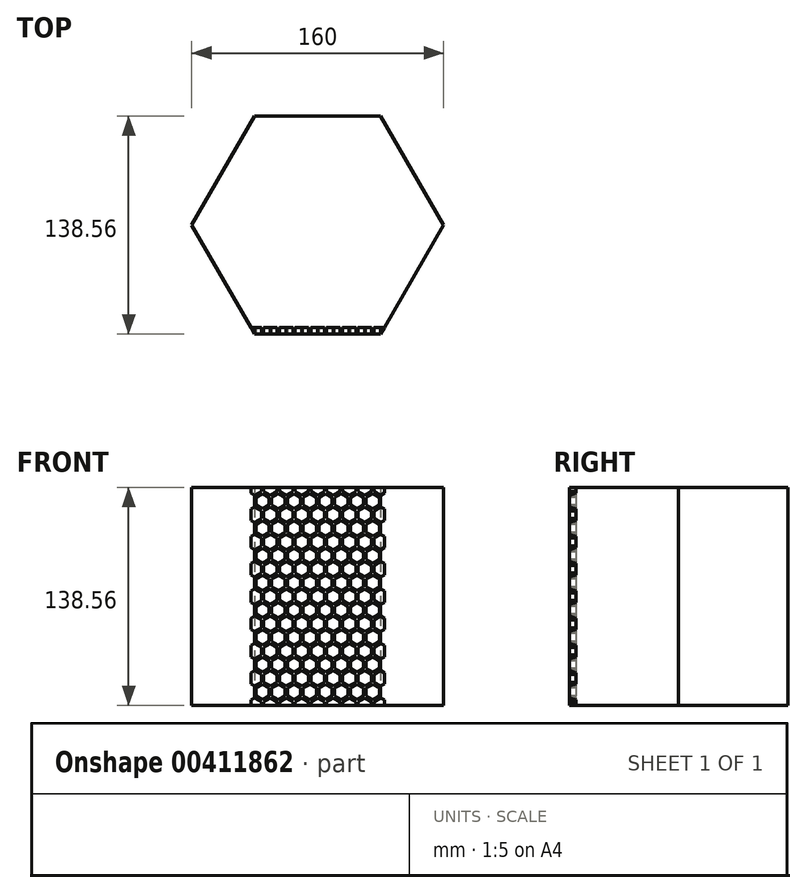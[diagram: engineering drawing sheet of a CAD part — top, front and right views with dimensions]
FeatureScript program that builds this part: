
annotation { "Feature Type Name" : "Feature", "Feature Type Description" : "" }
export const myFeature = defineFeature(function(context is Context, id is Id, definition is map)
    precondition{}
    {
        {
            var Q0;
            Q0=qCreatedBy(makeId("Top.planeOp"),FACE);
            var sketch = newSketch(context, id + "F0", { "sketchPlane" : qUnion([Q0])});
            skCircle(sketch, "E0.cCircle", {"center": v(0, 0) * mm, "radius": 69.28 * mm, "construction": true});
            skLineSegment(sketch, "E0.0", {"start": v(40, -69.28) * mm, "end": v(-40, -69.28) * mm});
            skLineSegment(sketch, "E0.1", {"start": v(-40, -69.28) * mm, "end": v(-80, 0) * mm});
            skLineSegment(sketch, "E0.2", {"start": v(-80, 0) * mm, "end": v(-40, 69.28) * mm});
            skLineSegment(sketch, "E0.3", {"start": v(-40, 69.28) * mm, "end": v(40, 69.28) * mm});
            skLineSegment(sketch, "E0.4", {"start": v(40, 69.28) * mm, "end": v(80, 0) * mm});
            skLineSegment(sketch, "E0.5", {"start": v(80, 0) * mm, "end": v(40, -69.28) * mm});
            skPoint(sketch, "E0.0.midPoint", {"position": v(0, -69.28) * mm});
            skSolve(sketch);
        }
        {
            var Q0;
            Q0=makeQuery(id+"F0.imprint","IMPRINT",FACE,{"disambiguationData":[TD([[makeQuery(id+"F0.imprint","IMPRINT",EDGE,{"derivedFrom":sQuery(id+"F0.wireOp",EDGE,"E0.0")}),-1.0]])]});
            extrude(context, id + "F1", {"entities" : qUnion([Q0]), "depth" : 138.56 * mm});
        }
        {
            var Q0;
            Q0=makeQuery(id+"F1.opExtrude","SWEPT_FACE",FACE,{"disambiguationData":[OSD([sQuery(id+"F0.wireOp",EDGE,"E0.0")])]});
            var sketch = newSketch(context, id + "F2", { "sketchPlane" : qUnion([Q0])});
            skCircle(sketch, "E1.cCircle", {"center": v(-40, 0) * mm, "radius": 4.25 * mm, "construction": true});
            skLineSegment(sketch, "E1.0", {"start": v(-35.75, 2.45) * mm, "end": v(-35.75, -2.45) * mm});
            skLineSegment(sketch, "E1.1", {"start": v(-35.75, -2.45) * mm, "end": v(-40, -4.9) * mm});
            skLineSegment(sketch, "E1.2", {"start": v(-40, -4.9) * mm, "end": v(-44.25, -2.45) * mm});
            skLineSegment(sketch, "E1.3", {"start": v(-44.25, -2.45) * mm, "end": v(-44.25, 2.45) * mm});
            skLineSegment(sketch, "E1.4", {"start": v(-44.25, 2.45) * mm, "end": v(-40, 4.9) * mm});
            skLineSegment(sketch, "E1.5", {"start": v(-40, 4.9) * mm, "end": v(-35.75, 2.45) * mm});
            skPoint(sketch, "E1.0.midPoint", {"position": v(-35.75, 0) * mm});
            skLineSegment(sketch, "E2.1.0.0", {"start": v(-34.25, 2.45) * mm, "end": v(-30, 4.9) * mm});
            skLineSegment(sketch, "E2.1.0.1", {"start": v(-30, 4.9) * mm, "end": v(-25.75, 2.45) * mm});
            skLineSegment(sketch, "E2.1.0.2", {"start": v(-25.75, 2.45) * mm, "end": v(-25.75, -2.45) * mm});
            skLineSegment(sketch, "E2.1.0.3", {"start": v(-25.75, -2.45) * mm, "end": v(-30, -4.9) * mm});
            skLineSegment(sketch, "E2.1.0.4", {"start": v(-30, -4.9) * mm, "end": v(-34.25, -2.45) * mm});
            skLineSegment(sketch, "E2.1.0.5", {"start": v(-34.25, -2.45) * mm, "end": v(-34.25, 2.45) * mm});
            skLineSegment(sketch, "E2.2.0.0", {"start": v(-24.25, 2.45) * mm, "end": v(-20, 4.9) * mm});
            skLineSegment(sketch, "E2.2.0.1", {"start": v(-20, 4.9) * mm, "end": v(-15.75, 2.45) * mm});
            skLineSegment(sketch, "E2.2.0.2", {"start": v(-15.75, 2.45) * mm, "end": v(-15.75, -2.45) * mm});
            skLineSegment(sketch, "E2.2.0.3", {"start": v(-15.75, -2.45) * mm, "end": v(-20, -4.9) * mm});
            skLineSegment(sketch, "E2.2.0.4", {"start": v(-20, -4.9) * mm, "end": v(-24.25, -2.45) * mm});
            skLineSegment(sketch, "E2.2.0.5", {"start": v(-24.25, -2.45) * mm, "end": v(-24.25, 2.45) * mm});
            skLineSegment(sketch, "E2.3.0.0", {"start": v(-14.25, 2.45) * mm, "end": v(-10, 4.9) * mm});
            skLineSegment(sketch, "E2.3.0.1", {"start": v(-10, 4.9) * mm, "end": v(-5.75, 2.45) * mm});
            skLineSegment(sketch, "E2.3.0.2", {"start": v(-5.75, 2.45) * mm, "end": v(-5.75, -2.45) * mm});
            skLineSegment(sketch, "E2.3.0.3", {"start": v(-5.75, -2.45) * mm, "end": v(-10, -4.9) * mm});
            skLineSegment(sketch, "E2.3.0.4", {"start": v(-10, -4.9) * mm, "end": v(-14.25, -2.45) * mm});
            skLineSegment(sketch, "E2.3.0.5", {"start": v(-14.25, -2.45) * mm, "end": v(-14.25, 2.45) * mm});
            skLineSegment(sketch, "E2.4.0.0", {"start": v(-4.25, 2.45) * mm, "end": v(0, 4.9) * mm});
            skLineSegment(sketch, "E2.4.0.1", {"start": v(0, 4.9) * mm, "end": v(4.25, 2.45) * mm});
            skLineSegment(sketch, "E2.4.0.2", {"start": v(4.25, 2.45) * mm, "end": v(4.25, -2.45) * mm});
            skLineSegment(sketch, "E2.4.0.3", {"start": v(4.25, -2.45) * mm, "end": v(0, -4.9) * mm});
            skLineSegment(sketch, "E2.4.0.4", {"start": v(0, -4.9) * mm, "end": v(-4.25, -2.45) * mm});
            skLineSegment(sketch, "E2.4.0.5", {"start": v(-4.25, -2.45) * mm, "end": v(-4.25, 2.45) * mm});
            skLineSegment(sketch, "E2.direction1", {"start": v(-44.25, -2.45) * mm, "end": v(-34.25, -2.45) * mm, "construction": true});
            skLineSegment(sketch, "E2.direction2", {"start": v(-44.25, -2.45) * mm, "end": v(-44.25, 14.87) * mm, "construction": true});
            skLineSegment(sketch, "E3.0.5.0", {"start": v(5.75, 2.45) * mm, "end": v(10, 4.9) * mm});
            skLineSegment(sketch, "E3.3.5.0", {"start": v(10, 4.9) * mm, "end": v(14.25, 2.45) * mm});
            skLineSegment(sketch, "E3.6.5.0", {"start": v(14.25, 2.45) * mm, "end": v(14.25, -2.45) * mm});
            skLineSegment(sketch, "E3.9.5.0", {"start": v(14.25, -2.45) * mm, "end": v(10, -4.9) * mm});
            skLineSegment(sketch, "E3.12.5.0", {"start": v(10, -4.9) * mm, "end": v(5.75, -2.45) * mm});
            skLineSegment(sketch, "E3.15.5.0", {"start": v(5.75, -2.45) * mm, "end": v(5.75, 2.45) * mm});
            skLineSegment(sketch, "E3.0.6.0", {"start": v(15.75, 2.45) * mm, "end": v(20, 4.9) * mm});
            skLineSegment(sketch, "E3.3.6.0", {"start": v(20, 4.9) * mm, "end": v(24.25, 2.45) * mm});
            skLineSegment(sketch, "E3.6.6.0", {"start": v(24.25, 2.45) * mm, "end": v(24.25, -2.45) * mm});
            skLineSegment(sketch, "E3.9.6.0", {"start": v(24.25, -2.45) * mm, "end": v(20, -4.9) * mm});
            skLineSegment(sketch, "E3.12.6.0", {"start": v(20, -4.9) * mm, "end": v(15.75, -2.45) * mm});
            skLineSegment(sketch, "E3.15.6.0", {"start": v(15.75, -2.45) * mm, "end": v(15.75, 2.45) * mm});
            skLineSegment(sketch, "E3.0.7.0", {"start": v(25.75, 2.45) * mm, "end": v(30, 4.9) * mm});
            skLineSegment(sketch, "E3.3.7.0", {"start": v(30, 4.9) * mm, "end": v(34.25, 2.45) * mm});
            skLineSegment(sketch, "E3.6.7.0", {"start": v(34.25, 2.45) * mm, "end": v(34.25, -2.45) * mm});
            skLineSegment(sketch, "E3.9.7.0", {"start": v(34.25, -2.45) * mm, "end": v(30, -4.9) * mm});
            skLineSegment(sketch, "E3.12.7.0", {"start": v(30, -4.9) * mm, "end": v(25.75, -2.45) * mm});
            skLineSegment(sketch, "E3.15.7.0", {"start": v(25.75, -2.45) * mm, "end": v(25.75, 2.45) * mm});
            skLineSegment(sketch, "E4.0.8.0", {"start": v(35.75, 2.45) * mm, "end": v(40, 4.9) * mm});
            skLineSegment(sketch, "E4.3.8.0", {"start": v(40, 4.9) * mm, "end": v(44.25, 2.45) * mm});
            skLineSegment(sketch, "E4.6.8.0", {"start": v(44.25, 2.45) * mm, "end": v(44.25, -2.45) * mm});
            skLineSegment(sketch, "E4.9.8.0", {"start": v(44.25, -2.45) * mm, "end": v(40, -4.9) * mm});
            skLineSegment(sketch, "E4.12.8.0", {"start": v(40, -4.9) * mm, "end": v(35.75, -2.45) * mm});
            skLineSegment(sketch, "E4.15.8.0", {"start": v(35.75, -2.45) * mm, "end": v(35.75, 2.45) * mm});
            skCircle(sketch, "E5.cCircle", {"center": v(-35, 8.66) * mm, "radius": 4.25 * mm, "construction": true});
            skLineSegment(sketch, "E5.0", {"start": v(-30.75, 11.11) * mm, "end": v(-30.75, 6.2) * mm});
            skLineSegment(sketch, "E5.1", {"start": v(-30.75, 6.2) * mm, "end": v(-35, 3.75) * mm});
            skLineSegment(sketch, "E5.2", {"start": v(-35, 3.75) * mm, "end": v(-39.25, 6.2) * mm});
            skLineSegment(sketch, "E5.3", {"start": v(-39.25, 6.2) * mm, "end": v(-39.25, 11.11) * mm});
            skLineSegment(sketch, "E5.4", {"start": v(-39.25, 11.11) * mm, "end": v(-35, 13.57) * mm});
            skLineSegment(sketch, "E5.5", {"start": v(-35, 13.57) * mm, "end": v(-30.75, 11.11) * mm});
            skPoint(sketch, "E5.0.midPoint", {"position": v(-30.75, 8.66) * mm});
            skLineSegment(sketch, "E6.0.0.1", {"start": v(-44.25, 19.77) * mm, "end": v(-40, 22.23) * mm});
            skLineSegment(sketch, "E6.3.0.1", {"start": v(-40, 22.23) * mm, "end": v(-35.75, 19.77) * mm});
            skLineSegment(sketch, "E6.6.0.1", {"start": v(-35.75, 19.77) * mm, "end": v(-35.75, 14.87) * mm});
            skLineSegment(sketch, "E6.9.0.1", {"start": v(-35.75, 14.87) * mm, "end": v(-40, 12.41) * mm});
            skLineSegment(sketch, "E6.12.0.1", {"start": v(-40, 12.41) * mm, "end": v(-44.25, 14.87) * mm});
            skLineSegment(sketch, "E6.15.0.1", {"start": v(-44.25, 14.87) * mm, "end": v(-44.25, 19.77) * mm});
            skLineSegment(sketch, "E6.0.0.2", {"start": v(-44.25, 37.1) * mm, "end": v(-40, 39.55) * mm});
            skLineSegment(sketch, "E6.3.0.2", {"start": v(-40, 39.55) * mm, "end": v(-35.75, 37.1) * mm});
            skLineSegment(sketch, "E6.6.0.2", {"start": v(-35.75, 37.1) * mm, "end": v(-35.75, 32.19) * mm});
            skLineSegment(sketch, "E6.9.0.2", {"start": v(-35.75, 32.19) * mm, "end": v(-40, 29.73) * mm});
            skLineSegment(sketch, "E6.12.0.2", {"start": v(-40, 29.73) * mm, "end": v(-44.25, 32.19) * mm});
            skLineSegment(sketch, "E6.15.0.2", {"start": v(-44.25, 32.19) * mm, "end": v(-44.25, 37.1) * mm});
            skLineSegment(sketch, "E6.0.0.3", {"start": v(-44.25, 54.42) * mm, "end": v(-40, 56.87) * mm});
            skLineSegment(sketch, "E6.3.0.3", {"start": v(-40, 56.87) * mm, "end": v(-35.75, 54.42) * mm});
            skLineSegment(sketch, "E6.6.0.3", {"start": v(-35.75, 54.42) * mm, "end": v(-35.75, 49.5) * mm});
            skLineSegment(sketch, "E6.9.0.3", {"start": v(-35.75, 49.5) * mm, "end": v(-40, 47.05) * mm});
            skLineSegment(sketch, "E6.12.0.3", {"start": v(-40, 47.05) * mm, "end": v(-44.25, 49.5) * mm});
            skLineSegment(sketch, "E6.15.0.3", {"start": v(-44.25, 49.5) * mm, "end": v(-44.25, 54.42) * mm});
            skLineSegment(sketch, "E6.0.0.4", {"start": v(-44.25, 71.74) * mm, "end": v(-40, 74.19) * mm});
            skLineSegment(sketch, "E6.3.0.4", {"start": v(-40, 74.19) * mm, "end": v(-35.75, 71.74) * mm});
            skLineSegment(sketch, "E6.6.0.4", {"start": v(-35.75, 71.74) * mm, "end": v(-35.75, 66.83) * mm});
            skLineSegment(sketch, "E6.9.0.4", {"start": v(-35.75, 66.83) * mm, "end": v(-40, 64.37) * mm});
            skLineSegment(sketch, "E6.12.0.4", {"start": v(-40, 64.37) * mm, "end": v(-44.25, 66.83) * mm});
            skLineSegment(sketch, "E6.15.0.4", {"start": v(-44.25, 66.83) * mm, "end": v(-44.25, 71.74) * mm});
            skLineSegment(sketch, "E6.0.0.5", {"start": v(-44.25, 89.06) * mm, "end": v(-40, 91.51) * mm});
            skLineSegment(sketch, "E6.3.0.5", {"start": v(-40, 91.51) * mm, "end": v(-35.75, 89.06) * mm});
            skLineSegment(sketch, "E6.6.0.5", {"start": v(-35.75, 89.06) * mm, "end": v(-35.75, 84.15) * mm});
            skLineSegment(sketch, "E6.9.0.5", {"start": v(-35.75, 84.15) * mm, "end": v(-40, 81.7) * mm});
            skLineSegment(sketch, "E6.12.0.5", {"start": v(-40, 81.7) * mm, "end": v(-44.25, 84.15) * mm});
            skLineSegment(sketch, "E6.15.0.5", {"start": v(-44.25, 84.15) * mm, "end": v(-44.25, 89.06) * mm});
            skLineSegment(sketch, "E6.0.0.6", {"start": v(-44.25, 106.38) * mm, "end": v(-40, 108.83) * mm});
            skLineSegment(sketch, "E6.3.0.6", {"start": v(-40, 108.83) * mm, "end": v(-35.75, 106.38) * mm});
            skLineSegment(sketch, "E6.6.0.6", {"start": v(-35.75, 106.38) * mm, "end": v(-35.75, 101.47) * mm});
            skLineSegment(sketch, "E6.9.0.6", {"start": v(-35.75, 101.47) * mm, "end": v(-40, 99.02) * mm});
            skLineSegment(sketch, "E6.12.0.6", {"start": v(-40, 99.02) * mm, "end": v(-44.25, 101.47) * mm});
            skLineSegment(sketch, "E6.15.0.6", {"start": v(-44.25, 101.47) * mm, "end": v(-44.25, 106.38) * mm});
            skLineSegment(sketch, "E6.0.0.7", {"start": v(-44.25, 123.7) * mm, "end": v(-40, 126.15) * mm});
            skLineSegment(sketch, "E6.3.0.7", {"start": v(-40, 126.15) * mm, "end": v(-35.75, 123.7) * mm});
            skLineSegment(sketch, "E6.6.0.7", {"start": v(-35.75, 123.7) * mm, "end": v(-35.75, 118.79) * mm});
            skLineSegment(sketch, "E6.9.0.7", {"start": v(-35.75, 118.79) * mm, "end": v(-40, 116.34) * mm});
            skLineSegment(sketch, "E6.12.0.7", {"start": v(-40, 116.34) * mm, "end": v(-44.25, 118.79) * mm});
            skLineSegment(sketch, "E6.15.0.7", {"start": v(-44.25, 118.79) * mm, "end": v(-44.25, 123.7) * mm});
            skLineSegment(sketch, "E6.0.0.8", {"start": v(-44.25, 141.02) * mm, "end": v(-40, 143.47) * mm});
            skLineSegment(sketch, "E6.3.0.8", {"start": v(-40, 143.47) * mm, "end": v(-35.75, 141.02) * mm});
            skLineSegment(sketch, "E6.6.0.8", {"start": v(-35.75, 141.02) * mm, "end": v(-35.75, 136.11) * mm});
            skLineSegment(sketch, "E6.9.0.8", {"start": v(-35.75, 136.11) * mm, "end": v(-40, 133.66) * mm});
            skLineSegment(sketch, "E6.12.0.8", {"start": v(-40, 133.66) * mm, "end": v(-44.25, 136.11) * mm});
            skLineSegment(sketch, "E6.15.0.8", {"start": v(-44.25, 136.11) * mm, "end": v(-44.25, 141.02) * mm});
            skLineSegment(sketch, "E6.0.1.1", {"start": v(-34.25, 19.77) * mm, "end": v(-30, 22.23) * mm});
            skLineSegment(sketch, "E6.3.1.1", {"start": v(-30, 22.23) * mm, "end": v(-25.75, 19.77) * mm});
            skLineSegment(sketch, "E6.6.1.1", {"start": v(-25.75, 19.77) * mm, "end": v(-25.75, 14.87) * mm});
            skLineSegment(sketch, "E6.9.1.1", {"start": v(-25.75, 14.87) * mm, "end": v(-30, 12.41) * mm});
            skLineSegment(sketch, "E6.12.1.1", {"start": v(-30, 12.41) * mm, "end": v(-34.25, 14.87) * mm});
            skLineSegment(sketch, "E6.15.1.1", {"start": v(-34.25, 14.87) * mm, "end": v(-34.25, 19.77) * mm});
            skLineSegment(sketch, "E6.0.1.2", {"start": v(-34.25, 37.1) * mm, "end": v(-30, 39.55) * mm});
            skLineSegment(sketch, "E6.3.1.2", {"start": v(-30, 39.55) * mm, "end": v(-25.75, 37.1) * mm});
            skLineSegment(sketch, "E6.6.1.2", {"start": v(-25.75, 37.1) * mm, "end": v(-25.75, 32.19) * mm});
            skLineSegment(sketch, "E6.9.1.2", {"start": v(-25.75, 32.19) * mm, "end": v(-30, 29.73) * mm});
            skLineSegment(sketch, "E6.12.1.2", {"start": v(-30, 29.73) * mm, "end": v(-34.25, 32.19) * mm});
            skLineSegment(sketch, "E6.15.1.2", {"start": v(-34.25, 32.19) * mm, "end": v(-34.25, 37.1) * mm});
            skLineSegment(sketch, "E6.0.1.3", {"start": v(-34.25, 54.42) * mm, "end": v(-30, 56.87) * mm});
            skLineSegment(sketch, "E6.3.1.3", {"start": v(-30, 56.87) * mm, "end": v(-25.75, 54.42) * mm});
            skLineSegment(sketch, "E6.6.1.3", {"start": v(-25.75, 54.42) * mm, "end": v(-25.75, 49.5) * mm});
            skLineSegment(sketch, "E6.9.1.3", {"start": v(-25.75, 49.5) * mm, "end": v(-30, 47.05) * mm});
            skLineSegment(sketch, "E6.12.1.3", {"start": v(-30, 47.05) * mm, "end": v(-34.25, 49.5) * mm});
            skLineSegment(sketch, "E6.15.1.3", {"start": v(-34.25, 49.5) * mm, "end": v(-34.25, 54.42) * mm});
            skLineSegment(sketch, "E6.0.1.4", {"start": v(-34.25, 71.74) * mm, "end": v(-30, 74.19) * mm});
            skLineSegment(sketch, "E6.3.1.4", {"start": v(-30, 74.19) * mm, "end": v(-25.75, 71.74) * mm});
            skLineSegment(sketch, "E6.6.1.4", {"start": v(-25.75, 71.74) * mm, "end": v(-25.75, 66.83) * mm});
            skLineSegment(sketch, "E6.9.1.4", {"start": v(-25.75, 66.83) * mm, "end": v(-30, 64.37) * mm});
            skLineSegment(sketch, "E6.12.1.4", {"start": v(-30, 64.37) * mm, "end": v(-34.25, 66.83) * mm});
            skLineSegment(sketch, "E6.15.1.4", {"start": v(-34.25, 66.83) * mm, "end": v(-34.25, 71.74) * mm});
            skLineSegment(sketch, "E6.0.1.5", {"start": v(-34.25, 89.06) * mm, "end": v(-30, 91.51) * mm});
            skLineSegment(sketch, "E6.3.1.5", {"start": v(-30, 91.51) * mm, "end": v(-25.75, 89.06) * mm});
            skLineSegment(sketch, "E6.6.1.5", {"start": v(-25.75, 89.06) * mm, "end": v(-25.75, 84.15) * mm});
            skLineSegment(sketch, "E6.9.1.5", {"start": v(-25.75, 84.15) * mm, "end": v(-30, 81.7) * mm});
            skLineSegment(sketch, "E6.12.1.5", {"start": v(-30, 81.7) * mm, "end": v(-34.25, 84.15) * mm});
            skLineSegment(sketch, "E6.15.1.5", {"start": v(-34.25, 84.15) * mm, "end": v(-34.25, 89.06) * mm});
            skLineSegment(sketch, "E6.0.1.6", {"start": v(-34.25, 106.38) * mm, "end": v(-30, 108.83) * mm});
            skLineSegment(sketch, "E6.3.1.6", {"start": v(-30, 108.83) * mm, "end": v(-25.75, 106.38) * mm});
            skLineSegment(sketch, "E6.6.1.6", {"start": v(-25.75, 106.38) * mm, "end": v(-25.75, 101.47) * mm});
            skLineSegment(sketch, "E6.9.1.6", {"start": v(-25.75, 101.47) * mm, "end": v(-30, 99.02) * mm});
            skLineSegment(sketch, "E6.12.1.6", {"start": v(-30, 99.02) * mm, "end": v(-34.25, 101.47) * mm});
            skLineSegment(sketch, "E6.15.1.6", {"start": v(-34.25, 101.47) * mm, "end": v(-34.25, 106.38) * mm});
            skLineSegment(sketch, "E6.0.1.7", {"start": v(-34.25, 123.7) * mm, "end": v(-30, 126.15) * mm});
            skLineSegment(sketch, "E6.3.1.7", {"start": v(-30, 126.15) * mm, "end": v(-25.75, 123.7) * mm});
            skLineSegment(sketch, "E6.6.1.7", {"start": v(-25.75, 123.7) * mm, "end": v(-25.75, 118.79) * mm});
            skLineSegment(sketch, "E6.9.1.7", {"start": v(-25.75, 118.79) * mm, "end": v(-30, 116.34) * mm});
            skLineSegment(sketch, "E6.12.1.7", {"start": v(-30, 116.34) * mm, "end": v(-34.25, 118.79) * mm});
            skLineSegment(sketch, "E6.15.1.7", {"start": v(-34.25, 118.79) * mm, "end": v(-34.25, 123.7) * mm});
            skLineSegment(sketch, "E6.0.1.8", {"start": v(-34.25, 141.02) * mm, "end": v(-30, 143.47) * mm});
            skLineSegment(sketch, "E6.3.1.8", {"start": v(-30, 143.47) * mm, "end": v(-25.75, 141.02) * mm});
            skLineSegment(sketch, "E6.6.1.8", {"start": v(-25.75, 141.02) * mm, "end": v(-25.75, 136.11) * mm});
            skLineSegment(sketch, "E6.9.1.8", {"start": v(-25.75, 136.11) * mm, "end": v(-30, 133.66) * mm});
            skLineSegment(sketch, "E6.12.1.8", {"start": v(-30, 133.66) * mm, "end": v(-34.25, 136.11) * mm});
            skLineSegment(sketch, "E6.15.1.8", {"start": v(-34.25, 136.11) * mm, "end": v(-34.25, 141.02) * mm});
            skLineSegment(sketch, "E6.0.2.1", {"start": v(-24.25, 19.77) * mm, "end": v(-20, 22.23) * mm});
            skLineSegment(sketch, "E6.3.2.1", {"start": v(-20, 22.23) * mm, "end": v(-15.75, 19.77) * mm});
            skLineSegment(sketch, "E6.6.2.1", {"start": v(-15.75, 19.77) * mm, "end": v(-15.75, 14.87) * mm});
            skLineSegment(sketch, "E6.9.2.1", {"start": v(-15.75, 14.87) * mm, "end": v(-20, 12.41) * mm});
            skLineSegment(sketch, "E6.12.2.1", {"start": v(-20, 12.41) * mm, "end": v(-24.25, 14.87) * mm});
            skLineSegment(sketch, "E6.15.2.1", {"start": v(-24.25, 14.87) * mm, "end": v(-24.25, 19.77) * mm});
            skLineSegment(sketch, "E6.0.2.2", {"start": v(-24.25, 37.1) * mm, "end": v(-20, 39.55) * mm});
            skLineSegment(sketch, "E6.3.2.2", {"start": v(-20, 39.55) * mm, "end": v(-15.75, 37.1) * mm});
            skLineSegment(sketch, "E6.6.2.2", {"start": v(-15.75, 37.1) * mm, "end": v(-15.75, 32.19) * mm});
            skLineSegment(sketch, "E6.9.2.2", {"start": v(-15.75, 32.19) * mm, "end": v(-20, 29.73) * mm});
            skLineSegment(sketch, "E6.12.2.2", {"start": v(-20, 29.73) * mm, "end": v(-24.25, 32.19) * mm});
            skLineSegment(sketch, "E6.15.2.2", {"start": v(-24.25, 32.19) * mm, "end": v(-24.25, 37.1) * mm});
            skLineSegment(sketch, "E6.0.2.3", {"start": v(-24.25, 54.42) * mm, "end": v(-20, 56.87) * mm});
            skLineSegment(sketch, "E6.3.2.3", {"start": v(-20, 56.87) * mm, "end": v(-15.75, 54.42) * mm});
            skLineSegment(sketch, "E6.6.2.3", {"start": v(-15.75, 54.42) * mm, "end": v(-15.75, 49.5) * mm});
            skLineSegment(sketch, "E6.9.2.3", {"start": v(-15.75, 49.5) * mm, "end": v(-20, 47.05) * mm});
            skLineSegment(sketch, "E6.12.2.3", {"start": v(-20, 47.05) * mm, "end": v(-24.25, 49.5) * mm});
            skLineSegment(sketch, "E6.15.2.3", {"start": v(-24.25, 49.5) * mm, "end": v(-24.25, 54.42) * mm});
            skLineSegment(sketch, "E6.0.2.4", {"start": v(-24.25, 71.74) * mm, "end": v(-20, 74.19) * mm});
            skLineSegment(sketch, "E6.3.2.4", {"start": v(-20, 74.19) * mm, "end": v(-15.75, 71.74) * mm});
            skLineSegment(sketch, "E6.6.2.4", {"start": v(-15.75, 71.74) * mm, "end": v(-15.75, 66.83) * mm});
            skLineSegment(sketch, "E6.9.2.4", {"start": v(-15.75, 66.83) * mm, "end": v(-20, 64.37) * mm});
            skLineSegment(sketch, "E6.12.2.4", {"start": v(-20, 64.37) * mm, "end": v(-24.25, 66.83) * mm});
            skLineSegment(sketch, "E6.15.2.4", {"start": v(-24.25, 66.83) * mm, "end": v(-24.25, 71.74) * mm});
            skLineSegment(sketch, "E6.0.2.5", {"start": v(-24.25, 89.06) * mm, "end": v(-20, 91.51) * mm});
            skLineSegment(sketch, "E6.3.2.5", {"start": v(-20, 91.51) * mm, "end": v(-15.75, 89.06) * mm});
            skLineSegment(sketch, "E6.6.2.5", {"start": v(-15.75, 89.06) * mm, "end": v(-15.75, 84.15) * mm});
            skLineSegment(sketch, "E6.9.2.5", {"start": v(-15.75, 84.15) * mm, "end": v(-20, 81.7) * mm});
            skLineSegment(sketch, "E6.12.2.5", {"start": v(-20, 81.7) * mm, "end": v(-24.25, 84.15) * mm});
            skLineSegment(sketch, "E6.15.2.5", {"start": v(-24.25, 84.15) * mm, "end": v(-24.25, 89.06) * mm});
            skLineSegment(sketch, "E6.0.2.6", {"start": v(-24.25, 106.38) * mm, "end": v(-20, 108.83) * mm});
            skLineSegment(sketch, "E6.3.2.6", {"start": v(-20, 108.83) * mm, "end": v(-15.75, 106.38) * mm});
            skLineSegment(sketch, "E6.6.2.6", {"start": v(-15.75, 106.38) * mm, "end": v(-15.75, 101.47) * mm});
            skLineSegment(sketch, "E6.9.2.6", {"start": v(-15.75, 101.47) * mm, "end": v(-20, 99.02) * mm});
            skLineSegment(sketch, "E6.12.2.6", {"start": v(-20, 99.02) * mm, "end": v(-24.25, 101.47) * mm});
            skLineSegment(sketch, "E6.15.2.6", {"start": v(-24.25, 101.47) * mm, "end": v(-24.25, 106.38) * mm});
            skLineSegment(sketch, "E6.0.2.7", {"start": v(-24.25, 123.7) * mm, "end": v(-20, 126.15) * mm});
            skLineSegment(sketch, "E6.3.2.7", {"start": v(-20, 126.15) * mm, "end": v(-15.75, 123.7) * mm});
            skLineSegment(sketch, "E6.6.2.7", {"start": v(-15.75, 123.7) * mm, "end": v(-15.75, 118.79) * mm});
            skLineSegment(sketch, "E6.9.2.7", {"start": v(-15.75, 118.79) * mm, "end": v(-20, 116.34) * mm});
            skLineSegment(sketch, "E6.12.2.7", {"start": v(-20, 116.34) * mm, "end": v(-24.25, 118.79) * mm});
            skLineSegment(sketch, "E6.15.2.7", {"start": v(-24.25, 118.79) * mm, "end": v(-24.25, 123.7) * mm});
            skLineSegment(sketch, "E6.0.2.8", {"start": v(-24.25, 141.02) * mm, "end": v(-20, 143.47) * mm});
            skLineSegment(sketch, "E6.3.2.8", {"start": v(-20, 143.47) * mm, "end": v(-15.75, 141.02) * mm});
            skLineSegment(sketch, "E6.6.2.8", {"start": v(-15.75, 141.02) * mm, "end": v(-15.75, 136.11) * mm});
            skLineSegment(sketch, "E6.9.2.8", {"start": v(-15.75, 136.11) * mm, "end": v(-20, 133.66) * mm});
            skLineSegment(sketch, "E6.12.2.8", {"start": v(-20, 133.66) * mm, "end": v(-24.25, 136.11) * mm});
            skLineSegment(sketch, "E6.15.2.8", {"start": v(-24.25, 136.11) * mm, "end": v(-24.25, 141.02) * mm});
            skLineSegment(sketch, "E6.0.3.1", {"start": v(-14.25, 19.77) * mm, "end": v(-10, 22.23) * mm});
            skLineSegment(sketch, "E6.3.3.1", {"start": v(-10, 22.23) * mm, "end": v(-5.75, 19.77) * mm});
            skLineSegment(sketch, "E6.6.3.1", {"start": v(-5.75, 19.77) * mm, "end": v(-5.75, 14.87) * mm});
            skLineSegment(sketch, "E6.9.3.1", {"start": v(-5.75, 14.87) * mm, "end": v(-10, 12.41) * mm});
            skLineSegment(sketch, "E6.12.3.1", {"start": v(-10, 12.41) * mm, "end": v(-14.25, 14.87) * mm});
            skLineSegment(sketch, "E6.15.3.1", {"start": v(-14.25, 14.87) * mm, "end": v(-14.25, 19.77) * mm});
            skLineSegment(sketch, "E6.0.3.2", {"start": v(-14.25, 37.1) * mm, "end": v(-10, 39.55) * mm});
            skLineSegment(sketch, "E6.3.3.2", {"start": v(-10, 39.55) * mm, "end": v(-5.75, 37.1) * mm});
            skLineSegment(sketch, "E6.6.3.2", {"start": v(-5.75, 37.1) * mm, "end": v(-5.75, 32.19) * mm});
            skLineSegment(sketch, "E6.9.3.2", {"start": v(-5.75, 32.19) * mm, "end": v(-10, 29.73) * mm});
            skLineSegment(sketch, "E6.12.3.2", {"start": v(-10, 29.73) * mm, "end": v(-14.25, 32.19) * mm});
            skLineSegment(sketch, "E6.15.3.2", {"start": v(-14.25, 32.19) * mm, "end": v(-14.25, 37.1) * mm});
            skLineSegment(sketch, "E6.0.3.3", {"start": v(-14.25, 54.42) * mm, "end": v(-10, 56.87) * mm});
            skLineSegment(sketch, "E6.3.3.3", {"start": v(-10, 56.87) * mm, "end": v(-5.75, 54.42) * mm});
            skLineSegment(sketch, "E6.6.3.3", {"start": v(-5.75, 54.42) * mm, "end": v(-5.75, 49.5) * mm});
            skLineSegment(sketch, "E6.9.3.3", {"start": v(-5.75, 49.5) * mm, "end": v(-10, 47.05) * mm});
            skLineSegment(sketch, "E6.12.3.3", {"start": v(-10, 47.05) * mm, "end": v(-14.25, 49.5) * mm});
            skLineSegment(sketch, "E6.15.3.3", {"start": v(-14.25, 49.5) * mm, "end": v(-14.25, 54.42) * mm});
            skLineSegment(sketch, "E6.0.3.4", {"start": v(-14.25, 71.74) * mm, "end": v(-10, 74.19) * mm});
            skLineSegment(sketch, "E6.3.3.4", {"start": v(-10, 74.19) * mm, "end": v(-5.75, 71.74) * mm});
            skLineSegment(sketch, "E6.6.3.4", {"start": v(-5.75, 71.74) * mm, "end": v(-5.75, 66.83) * mm});
            skLineSegment(sketch, "E6.9.3.4", {"start": v(-5.75, 66.83) * mm, "end": v(-10, 64.37) * mm});
            skLineSegment(sketch, "E6.12.3.4", {"start": v(-10, 64.37) * mm, "end": v(-14.25, 66.83) * mm});
            skLineSegment(sketch, "E6.15.3.4", {"start": v(-14.25, 66.83) * mm, "end": v(-14.25, 71.74) * mm});
            skLineSegment(sketch, "E6.0.3.5", {"start": v(-14.25, 89.06) * mm, "end": v(-10, 91.51) * mm});
            skLineSegment(sketch, "E6.3.3.5", {"start": v(-10, 91.51) * mm, "end": v(-5.75, 89.06) * mm});
            skLineSegment(sketch, "E6.6.3.5", {"start": v(-5.75, 89.06) * mm, "end": v(-5.75, 84.15) * mm});
            skLineSegment(sketch, "E6.9.3.5", {"start": v(-5.75, 84.15) * mm, "end": v(-10, 81.7) * mm});
            skLineSegment(sketch, "E6.12.3.5", {"start": v(-10, 81.7) * mm, "end": v(-14.25, 84.15) * mm});
            skLineSegment(sketch, "E6.15.3.5", {"start": v(-14.25, 84.15) * mm, "end": v(-14.25, 89.06) * mm});
            skLineSegment(sketch, "E6.0.3.6", {"start": v(-14.25, 106.38) * mm, "end": v(-10, 108.83) * mm});
            skLineSegment(sketch, "E6.3.3.6", {"start": v(-10, 108.83) * mm, "end": v(-5.75, 106.38) * mm});
            skLineSegment(sketch, "E6.6.3.6", {"start": v(-5.75, 106.38) * mm, "end": v(-5.75, 101.47) * mm});
            skLineSegment(sketch, "E6.9.3.6", {"start": v(-5.75, 101.47) * mm, "end": v(-10, 99.02) * mm});
            skLineSegment(sketch, "E6.12.3.6", {"start": v(-10, 99.02) * mm, "end": v(-14.25, 101.47) * mm});
            skLineSegment(sketch, "E6.15.3.6", {"start": v(-14.25, 101.47) * mm, "end": v(-14.25, 106.38) * mm});
            skLineSegment(sketch, "E6.0.3.7", {"start": v(-14.25, 123.7) * mm, "end": v(-10, 126.15) * mm});
            skLineSegment(sketch, "E6.3.3.7", {"start": v(-10, 126.15) * mm, "end": v(-5.75, 123.7) * mm});
            skLineSegment(sketch, "E6.6.3.7", {"start": v(-5.75, 123.7) * mm, "end": v(-5.75, 118.79) * mm});
            skLineSegment(sketch, "E6.9.3.7", {"start": v(-5.75, 118.79) * mm, "end": v(-10, 116.34) * mm});
            skLineSegment(sketch, "E6.12.3.7", {"start": v(-10, 116.34) * mm, "end": v(-14.25, 118.79) * mm});
            skLineSegment(sketch, "E6.15.3.7", {"start": v(-14.25, 118.79) * mm, "end": v(-14.25, 123.7) * mm});
            skLineSegment(sketch, "E6.0.3.8", {"start": v(-14.25, 141.02) * mm, "end": v(-10, 143.47) * mm});
            skLineSegment(sketch, "E6.3.3.8", {"start": v(-10, 143.47) * mm, "end": v(-5.75, 141.02) * mm});
            skLineSegment(sketch, "E6.6.3.8", {"start": v(-5.75, 141.02) * mm, "end": v(-5.75, 136.11) * mm});
            skLineSegment(sketch, "E6.9.3.8", {"start": v(-5.75, 136.11) * mm, "end": v(-10, 133.66) * mm});
            skLineSegment(sketch, "E6.12.3.8", {"start": v(-10, 133.66) * mm, "end": v(-14.25, 136.11) * mm});
            skLineSegment(sketch, "E6.15.3.8", {"start": v(-14.25, 136.11) * mm, "end": v(-14.25, 141.02) * mm});
            skLineSegment(sketch, "E6.0.4.1", {"start": v(-4.25, 19.77) * mm, "end": v(0, 22.23) * mm});
            skLineSegment(sketch, "E6.3.4.1", {"start": v(0, 22.23) * mm, "end": v(4.25, 19.77) * mm});
            skLineSegment(sketch, "E6.6.4.1", {"start": v(4.25, 19.77) * mm, "end": v(4.25, 14.87) * mm});
            skLineSegment(sketch, "E6.9.4.1", {"start": v(4.25, 14.87) * mm, "end": v(0, 12.41) * mm});
            skLineSegment(sketch, "E6.12.4.1", {"start": v(0, 12.41) * mm, "end": v(-4.25, 14.87) * mm});
            skLineSegment(sketch, "E6.15.4.1", {"start": v(-4.25, 14.87) * mm, "end": v(-4.25, 19.77) * mm});
            skLineSegment(sketch, "E6.0.4.2", {"start": v(-4.25, 37.1) * mm, "end": v(0, 39.55) * mm});
            skLineSegment(sketch, "E6.3.4.2", {"start": v(0, 39.55) * mm, "end": v(4.25, 37.1) * mm});
            skLineSegment(sketch, "E6.6.4.2", {"start": v(4.25, 37.1) * mm, "end": v(4.25, 32.19) * mm});
            skLineSegment(sketch, "E6.9.4.2", {"start": v(4.25, 32.19) * mm, "end": v(0, 29.73) * mm});
            skLineSegment(sketch, "E6.12.4.2", {"start": v(0, 29.73) * mm, "end": v(-4.25, 32.19) * mm});
            skLineSegment(sketch, "E6.15.4.2", {"start": v(-4.25, 32.19) * mm, "end": v(-4.25, 37.1) * mm});
            skLineSegment(sketch, "E6.0.4.3", {"start": v(-4.25, 54.42) * mm, "end": v(0, 56.87) * mm});
            skLineSegment(sketch, "E6.3.4.3", {"start": v(0, 56.87) * mm, "end": v(4.25, 54.42) * mm});
            skLineSegment(sketch, "E6.6.4.3", {"start": v(4.25, 54.42) * mm, "end": v(4.25, 49.5) * mm});
            skLineSegment(sketch, "E6.9.4.3", {"start": v(4.25, 49.5) * mm, "end": v(0, 47.05) * mm});
            skLineSegment(sketch, "E6.12.4.3", {"start": v(0, 47.05) * mm, "end": v(-4.25, 49.5) * mm});
            skLineSegment(sketch, "E6.15.4.3", {"start": v(-4.25, 49.5) * mm, "end": v(-4.25, 54.42) * mm});
            skLineSegment(sketch, "E6.0.4.4", {"start": v(-4.25, 71.74) * mm, "end": v(0, 74.19) * mm});
            skLineSegment(sketch, "E6.3.4.4", {"start": v(0, 74.19) * mm, "end": v(4.25, 71.74) * mm});
            skLineSegment(sketch, "E6.6.4.4", {"start": v(4.25, 71.74) * mm, "end": v(4.25, 66.83) * mm});
            skLineSegment(sketch, "E6.9.4.4", {"start": v(4.25, 66.83) * mm, "end": v(0, 64.37) * mm});
            skLineSegment(sketch, "E6.12.4.4", {"start": v(0, 64.37) * mm, "end": v(-4.25, 66.83) * mm});
            skLineSegment(sketch, "E6.15.4.4", {"start": v(-4.25, 66.83) * mm, "end": v(-4.25, 71.74) * mm});
            skLineSegment(sketch, "E6.0.4.5", {"start": v(-4.25, 89.06) * mm, "end": v(0, 91.51) * mm});
            skLineSegment(sketch, "E6.3.4.5", {"start": v(0, 91.51) * mm, "end": v(4.25, 89.06) * mm});
            skLineSegment(sketch, "E6.6.4.5", {"start": v(4.25, 89.06) * mm, "end": v(4.25, 84.15) * mm});
            skLineSegment(sketch, "E6.9.4.5", {"start": v(4.25, 84.15) * mm, "end": v(0, 81.7) * mm});
            skLineSegment(sketch, "E6.12.4.5", {"start": v(0, 81.7) * mm, "end": v(-4.25, 84.15) * mm});
            skLineSegment(sketch, "E6.15.4.5", {"start": v(-4.25, 84.15) * mm, "end": v(-4.25, 89.06) * mm});
            skLineSegment(sketch, "E6.0.4.6", {"start": v(-4.25, 106.38) * mm, "end": v(0, 108.83) * mm});
            skLineSegment(sketch, "E6.3.4.6", {"start": v(0, 108.83) * mm, "end": v(4.25, 106.38) * mm});
            skLineSegment(sketch, "E6.6.4.6", {"start": v(4.25, 106.38) * mm, "end": v(4.25, 101.47) * mm});
            skLineSegment(sketch, "E6.9.4.6", {"start": v(4.25, 101.47) * mm, "end": v(0, 99.02) * mm});
            skLineSegment(sketch, "E6.12.4.6", {"start": v(0, 99.02) * mm, "end": v(-4.25, 101.47) * mm});
            skLineSegment(sketch, "E6.15.4.6", {"start": v(-4.25, 101.47) * mm, "end": v(-4.25, 106.38) * mm});
            skLineSegment(sketch, "E6.0.4.7", {"start": v(-4.25, 123.7) * mm, "end": v(0, 126.15) * mm});
            skLineSegment(sketch, "E6.3.4.7", {"start": v(0, 126.15) * mm, "end": v(4.25, 123.7) * mm});
            skLineSegment(sketch, "E6.6.4.7", {"start": v(4.25, 123.7) * mm, "end": v(4.25, 118.79) * mm});
            skLineSegment(sketch, "E6.9.4.7", {"start": v(4.25, 118.79) * mm, "end": v(0, 116.34) * mm});
            skLineSegment(sketch, "E6.12.4.7", {"start": v(0, 116.34) * mm, "end": v(-4.25, 118.79) * mm});
            skLineSegment(sketch, "E6.15.4.7", {"start": v(-4.25, 118.79) * mm, "end": v(-4.25, 123.7) * mm});
            skLineSegment(sketch, "E6.0.4.8", {"start": v(-4.25, 141.02) * mm, "end": v(0, 143.47) * mm});
            skLineSegment(sketch, "E6.3.4.8", {"start": v(0, 143.47) * mm, "end": v(4.25, 141.02) * mm});
            skLineSegment(sketch, "E6.6.4.8", {"start": v(4.25, 141.02) * mm, "end": v(4.25, 136.11) * mm});
            skLineSegment(sketch, "E6.9.4.8", {"start": v(4.25, 136.11) * mm, "end": v(0, 133.66) * mm});
            skLineSegment(sketch, "E6.12.4.8", {"start": v(0, 133.66) * mm, "end": v(-4.25, 136.11) * mm});
            skLineSegment(sketch, "E6.15.4.8", {"start": v(-4.25, 136.11) * mm, "end": v(-4.25, 141.02) * mm});
            skLineSegment(sketch, "E6.0.5.1", {"start": v(5.75, 19.77) * mm, "end": v(10, 22.23) * mm});
            skLineSegment(sketch, "E6.3.5.1", {"start": v(10, 22.23) * mm, "end": v(14.25, 19.77) * mm});
            skLineSegment(sketch, "E6.6.5.1", {"start": v(14.25, 19.77) * mm, "end": v(14.25, 14.87) * mm});
            skLineSegment(sketch, "E6.9.5.1", {"start": v(14.25, 14.87) * mm, "end": v(10, 12.41) * mm});
            skLineSegment(sketch, "E6.12.5.1", {"start": v(10, 12.41) * mm, "end": v(5.75, 14.87) * mm});
            skLineSegment(sketch, "E6.15.5.1", {"start": v(5.75, 14.87) * mm, "end": v(5.75, 19.77) * mm});
            skLineSegment(sketch, "E6.0.5.2", {"start": v(5.75, 37.1) * mm, "end": v(10, 39.55) * mm});
            skLineSegment(sketch, "E6.3.5.2", {"start": v(10, 39.55) * mm, "end": v(14.25, 37.1) * mm});
            skLineSegment(sketch, "E6.6.5.2", {"start": v(14.25, 37.1) * mm, "end": v(14.25, 32.19) * mm});
            skLineSegment(sketch, "E6.9.5.2", {"start": v(14.25, 32.19) * mm, "end": v(10, 29.73) * mm});
            skLineSegment(sketch, "E6.12.5.2", {"start": v(10, 29.73) * mm, "end": v(5.75, 32.19) * mm});
            skLineSegment(sketch, "E6.15.5.2", {"start": v(5.75, 32.19) * mm, "end": v(5.75, 37.1) * mm});
            skLineSegment(sketch, "E6.0.5.3", {"start": v(5.75, 54.42) * mm, "end": v(10, 56.87) * mm});
            skLineSegment(sketch, "E6.3.5.3", {"start": v(10, 56.87) * mm, "end": v(14.25, 54.42) * mm});
            skLineSegment(sketch, "E6.6.5.3", {"start": v(14.25, 54.42) * mm, "end": v(14.25, 49.5) * mm});
            skLineSegment(sketch, "E6.9.5.3", {"start": v(14.25, 49.5) * mm, "end": v(10, 47.05) * mm});
            skLineSegment(sketch, "E6.12.5.3", {"start": v(10, 47.05) * mm, "end": v(5.75, 49.5) * mm});
            skLineSegment(sketch, "E6.15.5.3", {"start": v(5.75, 49.5) * mm, "end": v(5.75, 54.42) * mm});
            skLineSegment(sketch, "E6.0.5.4", {"start": v(5.75, 71.74) * mm, "end": v(10, 74.19) * mm});
            skLineSegment(sketch, "E6.3.5.4", {"start": v(10, 74.19) * mm, "end": v(14.25, 71.74) * mm});
            skLineSegment(sketch, "E6.6.5.4", {"start": v(14.25, 71.74) * mm, "end": v(14.25, 66.83) * mm});
            skLineSegment(sketch, "E6.9.5.4", {"start": v(14.25, 66.83) * mm, "end": v(10, 64.37) * mm});
            skLineSegment(sketch, "E6.12.5.4", {"start": v(10, 64.37) * mm, "end": v(5.75, 66.83) * mm});
            skLineSegment(sketch, "E6.15.5.4", {"start": v(5.75, 66.83) * mm, "end": v(5.75, 71.74) * mm});
            skLineSegment(sketch, "E6.0.5.5", {"start": v(5.75, 89.06) * mm, "end": v(10, 91.51) * mm});
            skLineSegment(sketch, "E6.3.5.5", {"start": v(10, 91.51) * mm, "end": v(14.25, 89.06) * mm});
            skLineSegment(sketch, "E6.6.5.5", {"start": v(14.25, 89.06) * mm, "end": v(14.25, 84.15) * mm});
            skLineSegment(sketch, "E6.9.5.5", {"start": v(14.25, 84.15) * mm, "end": v(10, 81.7) * mm});
            skLineSegment(sketch, "E6.12.5.5", {"start": v(10, 81.7) * mm, "end": v(5.75, 84.15) * mm});
            skLineSegment(sketch, "E6.15.5.5", {"start": v(5.75, 84.15) * mm, "end": v(5.75, 89.06) * mm});
            skLineSegment(sketch, "E6.0.5.6", {"start": v(5.75, 106.38) * mm, "end": v(10, 108.83) * mm});
            skLineSegment(sketch, "E6.3.5.6", {"start": v(10, 108.83) * mm, "end": v(14.25, 106.38) * mm});
            skLineSegment(sketch, "E6.6.5.6", {"start": v(14.25, 106.38) * mm, "end": v(14.25, 101.47) * mm});
            skLineSegment(sketch, "E6.9.5.6", {"start": v(14.25, 101.47) * mm, "end": v(10, 99.02) * mm});
            skLineSegment(sketch, "E6.12.5.6", {"start": v(10, 99.02) * mm, "end": v(5.75, 101.47) * mm});
            skLineSegment(sketch, "E6.15.5.6", {"start": v(5.75, 101.47) * mm, "end": v(5.75, 106.38) * mm});
            skLineSegment(sketch, "E6.0.5.7", {"start": v(5.75, 123.7) * mm, "end": v(10, 126.15) * mm});
            skLineSegment(sketch, "E6.3.5.7", {"start": v(10, 126.15) * mm, "end": v(14.25, 123.7) * mm});
            skLineSegment(sketch, "E6.6.5.7", {"start": v(14.25, 123.7) * mm, "end": v(14.25, 118.79) * mm});
            skLineSegment(sketch, "E6.9.5.7", {"start": v(14.25, 118.79) * mm, "end": v(10, 116.34) * mm});
            skLineSegment(sketch, "E6.12.5.7", {"start": v(10, 116.34) * mm, "end": v(5.75, 118.79) * mm});
            skLineSegment(sketch, "E6.15.5.7", {"start": v(5.75, 118.79) * mm, "end": v(5.75, 123.7) * mm});
            skLineSegment(sketch, "E6.0.5.8", {"start": v(5.75, 141.02) * mm, "end": v(10, 143.47) * mm});
            skLineSegment(sketch, "E6.3.5.8", {"start": v(10, 143.47) * mm, "end": v(14.25, 141.02) * mm});
            skLineSegment(sketch, "E6.6.5.8", {"start": v(14.25, 141.02) * mm, "end": v(14.25, 136.11) * mm});
            skLineSegment(sketch, "E6.9.5.8", {"start": v(14.25, 136.11) * mm, "end": v(10, 133.66) * mm});
            skLineSegment(sketch, "E6.12.5.8", {"start": v(10, 133.66) * mm, "end": v(5.75, 136.11) * mm});
            skLineSegment(sketch, "E6.15.5.8", {"start": v(5.75, 136.11) * mm, "end": v(5.75, 141.02) * mm});
            skLineSegment(sketch, "E6.0.6.1", {"start": v(15.75, 19.77) * mm, "end": v(20, 22.23) * mm});
            skLineSegment(sketch, "E6.3.6.1", {"start": v(20, 22.23) * mm, "end": v(24.25, 19.77) * mm});
            skLineSegment(sketch, "E6.6.6.1", {"start": v(24.25, 19.77) * mm, "end": v(24.25, 14.87) * mm});
            skLineSegment(sketch, "E6.9.6.1", {"start": v(24.25, 14.87) * mm, "end": v(20, 12.41) * mm});
            skLineSegment(sketch, "E6.12.6.1", {"start": v(20, 12.41) * mm, "end": v(15.75, 14.87) * mm});
            skLineSegment(sketch, "E6.15.6.1", {"start": v(15.75, 14.87) * mm, "end": v(15.75, 19.77) * mm});
            skLineSegment(sketch, "E6.0.6.2", {"start": v(15.75, 37.1) * mm, "end": v(20, 39.55) * mm});
            skLineSegment(sketch, "E6.3.6.2", {"start": v(20, 39.55) * mm, "end": v(24.25, 37.1) * mm});
            skLineSegment(sketch, "E6.6.6.2", {"start": v(24.25, 37.1) * mm, "end": v(24.25, 32.19) * mm});
            skLineSegment(sketch, "E6.9.6.2", {"start": v(24.25, 32.19) * mm, "end": v(20, 29.73) * mm});
            skLineSegment(sketch, "E6.12.6.2", {"start": v(20, 29.73) * mm, "end": v(15.75, 32.19) * mm});
            skLineSegment(sketch, "E6.15.6.2", {"start": v(15.75, 32.19) * mm, "end": v(15.75, 37.1) * mm});
            skLineSegment(sketch, "E6.0.6.3", {"start": v(15.75, 54.42) * mm, "end": v(20, 56.87) * mm});
            skLineSegment(sketch, "E6.3.6.3", {"start": v(20, 56.87) * mm, "end": v(24.25, 54.42) * mm});
            skLineSegment(sketch, "E6.6.6.3", {"start": v(24.25, 54.42) * mm, "end": v(24.25, 49.5) * mm});
            skLineSegment(sketch, "E6.9.6.3", {"start": v(24.25, 49.5) * mm, "end": v(20, 47.05) * mm});
            skLineSegment(sketch, "E6.12.6.3", {"start": v(20, 47.05) * mm, "end": v(15.75, 49.5) * mm});
            skLineSegment(sketch, "E6.15.6.3", {"start": v(15.75, 49.5) * mm, "end": v(15.75, 54.42) * mm});
            skLineSegment(sketch, "E6.0.6.4", {"start": v(15.75, 71.74) * mm, "end": v(20, 74.19) * mm});
            skLineSegment(sketch, "E6.3.6.4", {"start": v(20, 74.19) * mm, "end": v(24.25, 71.74) * mm});
            skLineSegment(sketch, "E6.6.6.4", {"start": v(24.25, 71.74) * mm, "end": v(24.25, 66.83) * mm});
            skLineSegment(sketch, "E6.9.6.4", {"start": v(24.25, 66.83) * mm, "end": v(20, 64.37) * mm});
            skLineSegment(sketch, "E6.12.6.4", {"start": v(20, 64.37) * mm, "end": v(15.75, 66.83) * mm});
            skLineSegment(sketch, "E6.15.6.4", {"start": v(15.75, 66.83) * mm, "end": v(15.75, 71.74) * mm});
            skLineSegment(sketch, "E6.0.6.5", {"start": v(15.75, 89.06) * mm, "end": v(20, 91.51) * mm});
            skLineSegment(sketch, "E6.3.6.5", {"start": v(20, 91.51) * mm, "end": v(24.25, 89.06) * mm});
            skLineSegment(sketch, "E6.6.6.5", {"start": v(24.25, 89.06) * mm, "end": v(24.25, 84.15) * mm});
            skLineSegment(sketch, "E6.9.6.5", {"start": v(24.25, 84.15) * mm, "end": v(20, 81.7) * mm});
            skLineSegment(sketch, "E6.12.6.5", {"start": v(20, 81.7) * mm, "end": v(15.75, 84.15) * mm});
            skLineSegment(sketch, "E6.15.6.5", {"start": v(15.75, 84.15) * mm, "end": v(15.75, 89.06) * mm});
            skLineSegment(sketch, "E6.0.6.6", {"start": v(15.75, 106.38) * mm, "end": v(20, 108.83) * mm});
            skLineSegment(sketch, "E6.3.6.6", {"start": v(20, 108.83) * mm, "end": v(24.25, 106.38) * mm});
            skLineSegment(sketch, "E6.6.6.6", {"start": v(24.25, 106.38) * mm, "end": v(24.25, 101.47) * mm});
            skLineSegment(sketch, "E6.9.6.6", {"start": v(24.25, 101.47) * mm, "end": v(20, 99.02) * mm});
            skLineSegment(sketch, "E6.12.6.6", {"start": v(20, 99.02) * mm, "end": v(15.75, 101.47) * mm});
            skLineSegment(sketch, "E6.15.6.6", {"start": v(15.75, 101.47) * mm, "end": v(15.75, 106.38) * mm});
            skLineSegment(sketch, "E6.0.6.7", {"start": v(15.75, 123.7) * mm, "end": v(20, 126.15) * mm});
            skLineSegment(sketch, "E6.3.6.7", {"start": v(20, 126.15) * mm, "end": v(24.25, 123.7) * mm});
            skLineSegment(sketch, "E6.6.6.7", {"start": v(24.25, 123.7) * mm, "end": v(24.25, 118.79) * mm});
            skLineSegment(sketch, "E6.9.6.7", {"start": v(24.25, 118.79) * mm, "end": v(20, 116.34) * mm});
            skLineSegment(sketch, "E6.12.6.7", {"start": v(20, 116.34) * mm, "end": v(15.75, 118.79) * mm});
            skLineSegment(sketch, "E6.15.6.7", {"start": v(15.75, 118.79) * mm, "end": v(15.75, 123.7) * mm});
            skLineSegment(sketch, "E6.0.6.8", {"start": v(15.75, 141.02) * mm, "end": v(20, 143.47) * mm});
            skLineSegment(sketch, "E6.3.6.8", {"start": v(20, 143.47) * mm, "end": v(24.25, 141.02) * mm});
            skLineSegment(sketch, "E6.6.6.8", {"start": v(24.25, 141.02) * mm, "end": v(24.25, 136.11) * mm});
            skLineSegment(sketch, "E6.9.6.8", {"start": v(24.25, 136.11) * mm, "end": v(20, 133.66) * mm});
            skLineSegment(sketch, "E6.12.6.8", {"start": v(20, 133.66) * mm, "end": v(15.75, 136.11) * mm});
            skLineSegment(sketch, "E6.15.6.8", {"start": v(15.75, 136.11) * mm, "end": v(15.75, 141.02) * mm});
            skLineSegment(sketch, "E6.0.7.1", {"start": v(25.75, 19.77) * mm, "end": v(30, 22.23) * mm});
            skLineSegment(sketch, "E6.3.7.1", {"start": v(30, 22.23) * mm, "end": v(34.25, 19.77) * mm});
            skLineSegment(sketch, "E6.6.7.1", {"start": v(34.25, 19.77) * mm, "end": v(34.25, 14.87) * mm});
            skLineSegment(sketch, "E6.9.7.1", {"start": v(34.25, 14.87) * mm, "end": v(30, 12.41) * mm});
            skLineSegment(sketch, "E6.12.7.1", {"start": v(30, 12.41) * mm, "end": v(25.75, 14.87) * mm});
            skLineSegment(sketch, "E6.15.7.1", {"start": v(25.75, 14.87) * mm, "end": v(25.75, 19.77) * mm});
            skLineSegment(sketch, "E6.0.7.2", {"start": v(25.75, 37.1) * mm, "end": v(30, 39.55) * mm});
            skLineSegment(sketch, "E6.3.7.2", {"start": v(30, 39.55) * mm, "end": v(34.25, 37.1) * mm});
            skLineSegment(sketch, "E6.6.7.2", {"start": v(34.25, 37.1) * mm, "end": v(34.25, 32.19) * mm});
            skLineSegment(sketch, "E6.9.7.2", {"start": v(34.25, 32.19) * mm, "end": v(30, 29.73) * mm});
            skLineSegment(sketch, "E6.12.7.2", {"start": v(30, 29.73) * mm, "end": v(25.75, 32.19) * mm});
            skLineSegment(sketch, "E6.15.7.2", {"start": v(25.75, 32.19) * mm, "end": v(25.75, 37.1) * mm});
            skLineSegment(sketch, "E6.0.7.3", {"start": v(25.75, 54.42) * mm, "end": v(30, 56.87) * mm});
            skLineSegment(sketch, "E6.3.7.3", {"start": v(30, 56.87) * mm, "end": v(34.25, 54.42) * mm});
            skLineSegment(sketch, "E6.6.7.3", {"start": v(34.25, 54.42) * mm, "end": v(34.25, 49.5) * mm});
            skLineSegment(sketch, "E6.9.7.3", {"start": v(34.25, 49.5) * mm, "end": v(30, 47.05) * mm});
            skLineSegment(sketch, "E6.12.7.3", {"start": v(30, 47.05) * mm, "end": v(25.75, 49.5) * mm});
            skLineSegment(sketch, "E6.15.7.3", {"start": v(25.75, 49.5) * mm, "end": v(25.75, 54.42) * mm});
            skLineSegment(sketch, "E6.0.7.4", {"start": v(25.75, 71.74) * mm, "end": v(30, 74.19) * mm});
            skLineSegment(sketch, "E6.3.7.4", {"start": v(30, 74.19) * mm, "end": v(34.25, 71.74) * mm});
            skLineSegment(sketch, "E6.6.7.4", {"start": v(34.25, 71.74) * mm, "end": v(34.25, 66.83) * mm});
            skLineSegment(sketch, "E6.9.7.4", {"start": v(34.25, 66.83) * mm, "end": v(30, 64.37) * mm});
            skLineSegment(sketch, "E6.12.7.4", {"start": v(30, 64.37) * mm, "end": v(25.75, 66.83) * mm});
            skLineSegment(sketch, "E6.15.7.4", {"start": v(25.75, 66.83) * mm, "end": v(25.75, 71.74) * mm});
            skLineSegment(sketch, "E6.0.7.5", {"start": v(25.75, 89.06) * mm, "end": v(30, 91.51) * mm});
            skLineSegment(sketch, "E6.3.7.5", {"start": v(30, 91.51) * mm, "end": v(34.25, 89.06) * mm});
            skLineSegment(sketch, "E6.6.7.5", {"start": v(34.25, 89.06) * mm, "end": v(34.25, 84.15) * mm});
            skLineSegment(sketch, "E6.9.7.5", {"start": v(34.25, 84.15) * mm, "end": v(30, 81.7) * mm});
            skLineSegment(sketch, "E6.12.7.5", {"start": v(30, 81.7) * mm, "end": v(25.75, 84.15) * mm});
            skLineSegment(sketch, "E6.15.7.5", {"start": v(25.75, 84.15) * mm, "end": v(25.75, 89.06) * mm});
            skLineSegment(sketch, "E6.0.7.6", {"start": v(25.75, 106.38) * mm, "end": v(30, 108.83) * mm});
            skLineSegment(sketch, "E6.3.7.6", {"start": v(30, 108.83) * mm, "end": v(34.25, 106.38) * mm});
            skLineSegment(sketch, "E6.6.7.6", {"start": v(34.25, 106.38) * mm, "end": v(34.25, 101.47) * mm});
            skLineSegment(sketch, "E6.9.7.6", {"start": v(34.25, 101.47) * mm, "end": v(30, 99.02) * mm});
            skLineSegment(sketch, "E6.12.7.6", {"start": v(30, 99.02) * mm, "end": v(25.75, 101.47) * mm});
            skLineSegment(sketch, "E6.15.7.6", {"start": v(25.75, 101.47) * mm, "end": v(25.75, 106.38) * mm});
            skLineSegment(sketch, "E6.0.7.7", {"start": v(25.75, 123.7) * mm, "end": v(30, 126.15) * mm});
            skLineSegment(sketch, "E6.3.7.7", {"start": v(30, 126.15) * mm, "end": v(34.25, 123.7) * mm});
            skLineSegment(sketch, "E6.6.7.7", {"start": v(34.25, 123.7) * mm, "end": v(34.25, 118.79) * mm});
            skLineSegment(sketch, "E6.9.7.7", {"start": v(34.25, 118.79) * mm, "end": v(30, 116.34) * mm});
            skLineSegment(sketch, "E6.12.7.7", {"start": v(30, 116.34) * mm, "end": v(25.75, 118.79) * mm});
            skLineSegment(sketch, "E6.15.7.7", {"start": v(25.75, 118.79) * mm, "end": v(25.75, 123.7) * mm});
            skLineSegment(sketch, "E6.0.7.8", {"start": v(25.75, 141.02) * mm, "end": v(30, 143.47) * mm});
            skLineSegment(sketch, "E6.3.7.8", {"start": v(30, 143.47) * mm, "end": v(34.25, 141.02) * mm});
            skLineSegment(sketch, "E6.6.7.8", {"start": v(34.25, 141.02) * mm, "end": v(34.25, 136.11) * mm});
            skLineSegment(sketch, "E6.9.7.8", {"start": v(34.25, 136.11) * mm, "end": v(30, 133.66) * mm});
            skLineSegment(sketch, "E6.12.7.8", {"start": v(30, 133.66) * mm, "end": v(25.75, 136.11) * mm});
            skLineSegment(sketch, "E6.15.7.8", {"start": v(25.75, 136.11) * mm, "end": v(25.75, 141.02) * mm});
            skLineSegment(sketch, "E6.0.8.1", {"start": v(35.75, 19.77) * mm, "end": v(40, 22.23) * mm});
            skLineSegment(sketch, "E6.3.8.1", {"start": v(40, 22.23) * mm, "end": v(44.25, 19.77) * mm});
            skLineSegment(sketch, "E6.6.8.1", {"start": v(44.25, 19.77) * mm, "end": v(44.25, 14.87) * mm});
            skLineSegment(sketch, "E6.9.8.1", {"start": v(44.25, 14.87) * mm, "end": v(40, 12.41) * mm});
            skLineSegment(sketch, "E6.12.8.1", {"start": v(40, 12.41) * mm, "end": v(35.75, 14.87) * mm});
            skLineSegment(sketch, "E6.15.8.1", {"start": v(35.75, 14.87) * mm, "end": v(35.75, 19.77) * mm});
            skLineSegment(sketch, "E6.0.8.2", {"start": v(35.75, 37.1) * mm, "end": v(40, 39.55) * mm});
            skLineSegment(sketch, "E6.3.8.2", {"start": v(40, 39.55) * mm, "end": v(44.25, 37.1) * mm});
            skLineSegment(sketch, "E6.6.8.2", {"start": v(44.25, 37.1) * mm, "end": v(44.25, 32.19) * mm});
            skLineSegment(sketch, "E6.9.8.2", {"start": v(44.25, 32.19) * mm, "end": v(40, 29.73) * mm});
            skLineSegment(sketch, "E6.12.8.2", {"start": v(40, 29.73) * mm, "end": v(35.75, 32.19) * mm});
            skLineSegment(sketch, "E6.15.8.2", {"start": v(35.75, 32.19) * mm, "end": v(35.75, 37.1) * mm});
            skLineSegment(sketch, "E6.0.8.3", {"start": v(35.75, 54.42) * mm, "end": v(40, 56.87) * mm});
            skLineSegment(sketch, "E6.3.8.3", {"start": v(40, 56.87) * mm, "end": v(44.25, 54.42) * mm});
            skLineSegment(sketch, "E6.6.8.3", {"start": v(44.25, 54.42) * mm, "end": v(44.25, 49.5) * mm});
            skLineSegment(sketch, "E6.9.8.3", {"start": v(44.25, 49.5) * mm, "end": v(40, 47.05) * mm});
            skLineSegment(sketch, "E6.12.8.3", {"start": v(40, 47.05) * mm, "end": v(35.75, 49.5) * mm});
            skLineSegment(sketch, "E6.15.8.3", {"start": v(35.75, 49.5) * mm, "end": v(35.75, 54.42) * mm});
            skLineSegment(sketch, "E6.0.8.4", {"start": v(35.75, 71.74) * mm, "end": v(40, 74.19) * mm});
            skLineSegment(sketch, "E6.3.8.4", {"start": v(40, 74.19) * mm, "end": v(44.25, 71.74) * mm});
            skLineSegment(sketch, "E6.6.8.4", {"start": v(44.25, 71.74) * mm, "end": v(44.25, 66.83) * mm});
            skLineSegment(sketch, "E6.9.8.4", {"start": v(44.25, 66.83) * mm, "end": v(40, 64.37) * mm});
            skLineSegment(sketch, "E6.12.8.4", {"start": v(40, 64.37) * mm, "end": v(35.75, 66.83) * mm});
            skLineSegment(sketch, "E6.15.8.4", {"start": v(35.75, 66.83) * mm, "end": v(35.75, 71.74) * mm});
            skLineSegment(sketch, "E6.0.8.5", {"start": v(35.75, 89.06) * mm, "end": v(40, 91.51) * mm});
            skLineSegment(sketch, "E6.3.8.5", {"start": v(40, 91.51) * mm, "end": v(44.25, 89.06) * mm});
            skLineSegment(sketch, "E6.6.8.5", {"start": v(44.25, 89.06) * mm, "end": v(44.25, 84.15) * mm});
            skLineSegment(sketch, "E6.9.8.5", {"start": v(44.25, 84.15) * mm, "end": v(40, 81.7) * mm});
            skLineSegment(sketch, "E6.12.8.5", {"start": v(40, 81.7) * mm, "end": v(35.75, 84.15) * mm});
            skLineSegment(sketch, "E6.15.8.5", {"start": v(35.75, 84.15) * mm, "end": v(35.75, 89.06) * mm});
            skLineSegment(sketch, "E6.0.8.6", {"start": v(35.75, 106.38) * mm, "end": v(40, 108.83) * mm});
            skLineSegment(sketch, "E6.3.8.6", {"start": v(40, 108.83) * mm, "end": v(44.25, 106.38) * mm});
            skLineSegment(sketch, "E6.6.8.6", {"start": v(44.25, 106.38) * mm, "end": v(44.25, 101.47) * mm});
            skLineSegment(sketch, "E6.9.8.6", {"start": v(44.25, 101.47) * mm, "end": v(40, 99.02) * mm});
            skLineSegment(sketch, "E6.12.8.6", {"start": v(40, 99.02) * mm, "end": v(35.75, 101.47) * mm});
            skLineSegment(sketch, "E6.15.8.6", {"start": v(35.75, 101.47) * mm, "end": v(35.75, 106.38) * mm});
            skLineSegment(sketch, "E6.0.8.7", {"start": v(35.75, 123.7) * mm, "end": v(40, 126.15) * mm});
            skLineSegment(sketch, "E6.3.8.7", {"start": v(40, 126.15) * mm, "end": v(44.25, 123.7) * mm});
            skLineSegment(sketch, "E6.6.8.7", {"start": v(44.25, 123.7) * mm, "end": v(44.25, 118.79) * mm});
            skLineSegment(sketch, "E6.9.8.7", {"start": v(44.25, 118.79) * mm, "end": v(40, 116.34) * mm});
            skLineSegment(sketch, "E6.12.8.7", {"start": v(40, 116.34) * mm, "end": v(35.75, 118.79) * mm});
            skLineSegment(sketch, "E6.15.8.7", {"start": v(35.75, 118.79) * mm, "end": v(35.75, 123.7) * mm});
            skLineSegment(sketch, "E6.0.8.8", {"start": v(35.75, 141.02) * mm, "end": v(40, 143.47) * mm});
            skLineSegment(sketch, "E6.3.8.8", {"start": v(40, 143.47) * mm, "end": v(44.25, 141.02) * mm});
            skLineSegment(sketch, "E6.6.8.8", {"start": v(44.25, 141.02) * mm, "end": v(44.25, 136.11) * mm});
            skLineSegment(sketch, "E6.9.8.8", {"start": v(44.25, 136.11) * mm, "end": v(40, 133.66) * mm});
            skLineSegment(sketch, "E6.12.8.8", {"start": v(40, 133.66) * mm, "end": v(35.75, 136.11) * mm});
            skLineSegment(sketch, "E6.15.8.8", {"start": v(35.75, 136.11) * mm, "end": v(35.75, 141.02) * mm});
            skLineSegment(sketch, "E7.0.1.0", {"start": v(-30.75, 23.53) * mm, "end": v(-35, 21.07) * mm});
            skLineSegment(sketch, "E7.0.1.1", {"start": v(-30.75, 28.43) * mm, "end": v(-30.75, 23.53) * mm});
            skLineSegment(sketch, "E7.0.1.2", {"start": v(-35, 30.89) * mm, "end": v(-30.75, 28.43) * mm});
            skLineSegment(sketch, "E7.0.1.3", {"start": v(-39.25, 28.43) * mm, "end": v(-35, 30.89) * mm});
            skLineSegment(sketch, "E7.0.1.4", {"start": v(-39.25, 23.53) * mm, "end": v(-39.25, 28.43) * mm});
            skLineSegment(sketch, "E7.0.1.5", {"start": v(-35, 21.07) * mm, "end": v(-39.25, 23.53) * mm});
            skLineSegment(sketch, "E7.0.2.0", {"start": v(-30.75, 40.85) * mm, "end": v(-35, 38.4) * mm});
            skLineSegment(sketch, "E7.0.2.1", {"start": v(-30.75, 45.76) * mm, "end": v(-30.75, 40.85) * mm});
            skLineSegment(sketch, "E7.0.2.2", {"start": v(-35, 48.2) * mm, "end": v(-30.75, 45.76) * mm});
            skLineSegment(sketch, "E7.0.2.3", {"start": v(-39.25, 45.76) * mm, "end": v(-35, 48.2) * mm});
            skLineSegment(sketch, "E7.0.2.4", {"start": v(-39.25, 40.85) * mm, "end": v(-39.25, 45.76) * mm});
            skLineSegment(sketch, "E7.0.2.5", {"start": v(-35, 38.4) * mm, "end": v(-39.25, 40.85) * mm});
            skLineSegment(sketch, "E7.0.3.0", {"start": v(-30.75, 58.17) * mm, "end": v(-35, 55.71) * mm});
            skLineSegment(sketch, "E7.0.3.1", {"start": v(-30.75, 63.08) * mm, "end": v(-30.75, 58.17) * mm});
            skLineSegment(sketch, "E7.0.3.2", {"start": v(-35, 65.53) * mm, "end": v(-30.75, 63.08) * mm});
            skLineSegment(sketch, "E7.0.3.3", {"start": v(-39.25, 63.08) * mm, "end": v(-35, 65.53) * mm});
            skLineSegment(sketch, "E7.0.3.4", {"start": v(-39.25, 58.17) * mm, "end": v(-39.25, 63.08) * mm});
            skLineSegment(sketch, "E7.0.3.5", {"start": v(-35, 55.71) * mm, "end": v(-39.25, 58.17) * mm});
            skLineSegment(sketch, "E7.0.4.0", {"start": v(-30.75, 75.49) * mm, "end": v(-35, 73.03) * mm});
            skLineSegment(sketch, "E7.0.4.1", {"start": v(-30.75, 80.4) * mm, "end": v(-30.75, 75.49) * mm});
            skLineSegment(sketch, "E7.0.4.2", {"start": v(-35, 82.85) * mm, "end": v(-30.75, 80.4) * mm});
            skLineSegment(sketch, "E7.0.4.3", {"start": v(-39.25, 80.4) * mm, "end": v(-35, 82.85) * mm});
            skLineSegment(sketch, "E7.0.4.4", {"start": v(-39.25, 75.49) * mm, "end": v(-39.25, 80.4) * mm});
            skLineSegment(sketch, "E7.0.4.5", {"start": v(-35, 73.03) * mm, "end": v(-39.25, 75.49) * mm});
            skLineSegment(sketch, "E7.1.0.0", {"start": v(-20.75, 6.2) * mm, "end": v(-25, 3.75) * mm});
            skLineSegment(sketch, "E7.1.0.1", {"start": v(-20.75, 11.11) * mm, "end": v(-20.75, 6.2) * mm});
            skLineSegment(sketch, "E7.1.0.2", {"start": v(-25, 13.57) * mm, "end": v(-20.75, 11.11) * mm});
            skLineSegment(sketch, "E7.1.0.3", {"start": v(-29.25, 11.11) * mm, "end": v(-25, 13.57) * mm});
            skLineSegment(sketch, "E7.1.0.4", {"start": v(-29.25, 6.2) * mm, "end": v(-29.25, 11.11) * mm});
            skLineSegment(sketch, "E7.1.0.5", {"start": v(-25, 3.75) * mm, "end": v(-29.25, 6.2) * mm});
            skLineSegment(sketch, "E7.1.1.0", {"start": v(-20.75, 23.53) * mm, "end": v(-25, 21.07) * mm});
            skLineSegment(sketch, "E7.1.1.1", {"start": v(-20.75, 28.43) * mm, "end": v(-20.75, 23.53) * mm});
            skLineSegment(sketch, "E7.1.1.2", {"start": v(-25, 30.89) * mm, "end": v(-20.75, 28.43) * mm});
            skLineSegment(sketch, "E7.1.1.3", {"start": v(-29.25, 28.43) * mm, "end": v(-25, 30.89) * mm});
            skLineSegment(sketch, "E7.1.1.4", {"start": v(-29.25, 23.53) * mm, "end": v(-29.25, 28.43) * mm});
            skLineSegment(sketch, "E7.1.1.5", {"start": v(-25, 21.07) * mm, "end": v(-29.25, 23.53) * mm});
            skLineSegment(sketch, "E7.1.2.0", {"start": v(-20.75, 40.85) * mm, "end": v(-25, 38.4) * mm});
            skLineSegment(sketch, "E7.1.2.1", {"start": v(-20.75, 45.76) * mm, "end": v(-20.75, 40.85) * mm});
            skLineSegment(sketch, "E7.1.2.2", {"start": v(-25, 48.2) * mm, "end": v(-20.75, 45.76) * mm});
            skLineSegment(sketch, "E7.1.2.3", {"start": v(-29.25, 45.76) * mm, "end": v(-25, 48.2) * mm});
            skLineSegment(sketch, "E7.1.2.4", {"start": v(-29.25, 40.85) * mm, "end": v(-29.25, 45.76) * mm});
            skLineSegment(sketch, "E7.1.2.5", {"start": v(-25, 38.4) * mm, "end": v(-29.25, 40.85) * mm});
            skLineSegment(sketch, "E7.1.3.0", {"start": v(-20.75, 58.17) * mm, "end": v(-25, 55.71) * mm});
            skLineSegment(sketch, "E7.1.3.1", {"start": v(-20.75, 63.08) * mm, "end": v(-20.75, 58.17) * mm});
            skLineSegment(sketch, "E7.1.3.2", {"start": v(-25, 65.53) * mm, "end": v(-20.75, 63.08) * mm});
            skLineSegment(sketch, "E7.1.3.3", {"start": v(-29.25, 63.08) * mm, "end": v(-25, 65.53) * mm});
            skLineSegment(sketch, "E7.1.3.4", {"start": v(-29.25, 58.17) * mm, "end": v(-29.25, 63.08) * mm});
            skLineSegment(sketch, "E7.1.3.5", {"start": v(-25, 55.71) * mm, "end": v(-29.25, 58.17) * mm});
            skLineSegment(sketch, "E7.1.4.0", {"start": v(-20.75, 75.49) * mm, "end": v(-25, 73.03) * mm});
            skLineSegment(sketch, "E7.1.4.1", {"start": v(-20.75, 80.4) * mm, "end": v(-20.75, 75.49) * mm});
            skLineSegment(sketch, "E7.1.4.2", {"start": v(-25, 82.85) * mm, "end": v(-20.75, 80.4) * mm});
            skLineSegment(sketch, "E7.1.4.3", {"start": v(-29.25, 80.4) * mm, "end": v(-25, 82.85) * mm});
            skLineSegment(sketch, "E7.1.4.4", {"start": v(-29.25, 75.49) * mm, "end": v(-29.25, 80.4) * mm});
            skLineSegment(sketch, "E7.1.4.5", {"start": v(-25, 73.03) * mm, "end": v(-29.25, 75.49) * mm});
            skLineSegment(sketch, "E7.2.0.0", {"start": v(-10.75, 6.2) * mm, "end": v(-15, 3.75) * mm});
            skLineSegment(sketch, "E7.2.0.1", {"start": v(-10.75, 11.11) * mm, "end": v(-10.75, 6.2) * mm});
            skLineSegment(sketch, "E7.2.0.2", {"start": v(-15, 13.57) * mm, "end": v(-10.75, 11.11) * mm});
            skLineSegment(sketch, "E7.2.0.3", {"start": v(-19.25, 11.11) * mm, "end": v(-15, 13.57) * mm});
            skLineSegment(sketch, "E7.2.0.4", {"start": v(-19.25, 6.2) * mm, "end": v(-19.25, 11.11) * mm});
            skLineSegment(sketch, "E7.2.0.5", {"start": v(-15, 3.75) * mm, "end": v(-19.25, 6.2) * mm});
            skLineSegment(sketch, "E7.2.1.0", {"start": v(-10.75, 23.53) * mm, "end": v(-15, 21.07) * mm});
            skLineSegment(sketch, "E7.2.1.1", {"start": v(-10.75, 28.43) * mm, "end": v(-10.75, 23.53) * mm});
            skLineSegment(sketch, "E7.2.1.2", {"start": v(-15, 30.89) * mm, "end": v(-10.75, 28.43) * mm});
            skLineSegment(sketch, "E7.2.1.3", {"start": v(-19.25, 28.43) * mm, "end": v(-15, 30.89) * mm});
            skLineSegment(sketch, "E7.2.1.4", {"start": v(-19.25, 23.53) * mm, "end": v(-19.25, 28.43) * mm});
            skLineSegment(sketch, "E7.2.1.5", {"start": v(-15, 21.07) * mm, "end": v(-19.25, 23.53) * mm});
            skLineSegment(sketch, "E7.2.2.0", {"start": v(-10.75, 40.85) * mm, "end": v(-15, 38.4) * mm});
            skLineSegment(sketch, "E7.2.2.1", {"start": v(-10.75, 45.76) * mm, "end": v(-10.75, 40.85) * mm});
            skLineSegment(sketch, "E7.2.2.2", {"start": v(-15, 48.2) * mm, "end": v(-10.75, 45.76) * mm});
            skLineSegment(sketch, "E7.2.2.3", {"start": v(-19.25, 45.76) * mm, "end": v(-15, 48.2) * mm});
            skLineSegment(sketch, "E7.2.2.4", {"start": v(-19.25, 40.85) * mm, "end": v(-19.25, 45.76) * mm});
            skLineSegment(sketch, "E7.2.2.5", {"start": v(-15, 38.4) * mm, "end": v(-19.25, 40.85) * mm});
            skLineSegment(sketch, "E7.2.3.0", {"start": v(-10.75, 58.17) * mm, "end": v(-15, 55.71) * mm});
            skLineSegment(sketch, "E7.2.3.1", {"start": v(-10.75, 63.08) * mm, "end": v(-10.75, 58.17) * mm});
            skLineSegment(sketch, "E7.2.3.2", {"start": v(-15, 65.53) * mm, "end": v(-10.75, 63.08) * mm});
            skLineSegment(sketch, "E7.2.3.3", {"start": v(-19.25, 63.08) * mm, "end": v(-15, 65.53) * mm});
            skLineSegment(sketch, "E7.2.3.4", {"start": v(-19.25, 58.17) * mm, "end": v(-19.25, 63.08) * mm});
            skLineSegment(sketch, "E7.2.3.5", {"start": v(-15, 55.71) * mm, "end": v(-19.25, 58.17) * mm});
            skLineSegment(sketch, "E7.2.4.0", {"start": v(-10.75, 75.49) * mm, "end": v(-15, 73.03) * mm});
            skLineSegment(sketch, "E7.2.4.1", {"start": v(-10.75, 80.4) * mm, "end": v(-10.75, 75.49) * mm});
            skLineSegment(sketch, "E7.2.4.2", {"start": v(-15, 82.85) * mm, "end": v(-10.75, 80.4) * mm});
            skLineSegment(sketch, "E7.2.4.3", {"start": v(-19.25, 80.4) * mm, "end": v(-15, 82.85) * mm});
            skLineSegment(sketch, "E7.2.4.4", {"start": v(-19.25, 75.49) * mm, "end": v(-19.25, 80.4) * mm});
            skLineSegment(sketch, "E7.2.4.5", {"start": v(-15, 73.03) * mm, "end": v(-19.25, 75.49) * mm});
            skLineSegment(sketch, "E7.3.0.0", {"start": v(-0.75, 6.2) * mm, "end": v(-5, 3.75) * mm});
            skLineSegment(sketch, "E7.3.0.1", {"start": v(-0.75, 11.11) * mm, "end": v(-0.75, 6.2) * mm});
            skLineSegment(sketch, "E7.3.0.2", {"start": v(-5, 13.57) * mm, "end": v(-0.75, 11.11) * mm});
            skLineSegment(sketch, "E7.3.0.3", {"start": v(-9.25, 11.11) * mm, "end": v(-5, 13.57) * mm});
            skLineSegment(sketch, "E7.3.0.4", {"start": v(-9.25, 6.2) * mm, "end": v(-9.25, 11.11) * mm});
            skLineSegment(sketch, "E7.3.0.5", {"start": v(-5, 3.75) * mm, "end": v(-9.25, 6.2) * mm});
            skLineSegment(sketch, "E7.3.1.0", {"start": v(-0.75, 23.53) * mm, "end": v(-5, 21.07) * mm});
            skLineSegment(sketch, "E7.3.1.1", {"start": v(-0.75, 28.43) * mm, "end": v(-0.75, 23.53) * mm});
            skLineSegment(sketch, "E7.3.1.2", {"start": v(-5, 30.89) * mm, "end": v(-0.75, 28.43) * mm});
            skLineSegment(sketch, "E7.3.1.3", {"start": v(-9.25, 28.43) * mm, "end": v(-5, 30.89) * mm});
            skLineSegment(sketch, "E7.3.1.4", {"start": v(-9.25, 23.53) * mm, "end": v(-9.25, 28.43) * mm});
            skLineSegment(sketch, "E7.3.1.5", {"start": v(-5, 21.07) * mm, "end": v(-9.25, 23.53) * mm});
            skLineSegment(sketch, "E7.3.2.0", {"start": v(-0.75, 40.85) * mm, "end": v(-5, 38.4) * mm});
            skLineSegment(sketch, "E7.3.2.1", {"start": v(-0.75, 45.76) * mm, "end": v(-0.75, 40.85) * mm});
            skLineSegment(sketch, "E7.3.2.2", {"start": v(-5, 48.2) * mm, "end": v(-0.75, 45.76) * mm});
            skLineSegment(sketch, "E7.3.2.3", {"start": v(-9.25, 45.76) * mm, "end": v(-5, 48.2) * mm});
            skLineSegment(sketch, "E7.3.2.4", {"start": v(-9.25, 40.85) * mm, "end": v(-9.25, 45.76) * mm});
            skLineSegment(sketch, "E7.3.2.5", {"start": v(-5, 38.4) * mm, "end": v(-9.25, 40.85) * mm});
            skLineSegment(sketch, "E7.3.3.0", {"start": v(-0.75, 58.17) * mm, "end": v(-5, 55.71) * mm});
            skLineSegment(sketch, "E7.3.3.1", {"start": v(-0.75, 63.08) * mm, "end": v(-0.75, 58.17) * mm});
            skLineSegment(sketch, "E7.3.3.2", {"start": v(-5, 65.53) * mm, "end": v(-0.75, 63.08) * mm});
            skLineSegment(sketch, "E7.3.3.3", {"start": v(-9.25, 63.08) * mm, "end": v(-5, 65.53) * mm});
            skLineSegment(sketch, "E7.3.3.4", {"start": v(-9.25, 58.17) * mm, "end": v(-9.25, 63.08) * mm});
            skLineSegment(sketch, "E7.3.3.5", {"start": v(-5, 55.71) * mm, "end": v(-9.25, 58.17) * mm});
            skLineSegment(sketch, "E7.3.4.0", {"start": v(-0.75, 75.49) * mm, "end": v(-5, 73.03) * mm});
            skLineSegment(sketch, "E7.3.4.1", {"start": v(-0.75, 80.4) * mm, "end": v(-0.75, 75.49) * mm});
            skLineSegment(sketch, "E7.3.4.2", {"start": v(-5, 82.85) * mm, "end": v(-0.75, 80.4) * mm});
            skLineSegment(sketch, "E7.3.4.3", {"start": v(-9.25, 80.4) * mm, "end": v(-5, 82.85) * mm});
            skLineSegment(sketch, "E7.3.4.4", {"start": v(-9.25, 75.49) * mm, "end": v(-9.25, 80.4) * mm});
            skLineSegment(sketch, "E7.3.4.5", {"start": v(-5, 73.03) * mm, "end": v(-9.25, 75.49) * mm});
            skLineSegment(sketch, "E7.4.0.0", {"start": v(9.25, 6.2) * mm, "end": v(5, 3.75) * mm});
            skLineSegment(sketch, "E7.4.0.1", {"start": v(9.25, 11.11) * mm, "end": v(9.25, 6.2) * mm});
            skLineSegment(sketch, "E7.4.0.2", {"start": v(5, 13.57) * mm, "end": v(9.25, 11.11) * mm});
            skLineSegment(sketch, "E7.4.0.3", {"start": v(0.75, 11.11) * mm, "end": v(5, 13.57) * mm});
            skLineSegment(sketch, "E7.4.0.4", {"start": v(0.75, 6.2) * mm, "end": v(0.75, 11.11) * mm});
            skLineSegment(sketch, "E7.4.0.5", {"start": v(5, 3.75) * mm, "end": v(0.75, 6.2) * mm});
            skLineSegment(sketch, "E7.4.1.0", {"start": v(9.25, 23.53) * mm, "end": v(5, 21.07) * mm});
            skLineSegment(sketch, "E7.4.1.1", {"start": v(9.25, 28.43) * mm, "end": v(9.25, 23.53) * mm});
            skLineSegment(sketch, "E7.4.1.2", {"start": v(5, 30.89) * mm, "end": v(9.25, 28.43) * mm});
            skLineSegment(sketch, "E7.4.1.3", {"start": v(0.75, 28.43) * mm, "end": v(5, 30.89) * mm});
            skLineSegment(sketch, "E7.4.1.4", {"start": v(0.75, 23.53) * mm, "end": v(0.75, 28.43) * mm});
            skLineSegment(sketch, "E7.4.1.5", {"start": v(5, 21.07) * mm, "end": v(0.75, 23.53) * mm});
            skLineSegment(sketch, "E7.4.2.0", {"start": v(9.25, 40.85) * mm, "end": v(5, 38.4) * mm});
            skLineSegment(sketch, "E7.4.2.1", {"start": v(9.25, 45.76) * mm, "end": v(9.25, 40.85) * mm});
            skLineSegment(sketch, "E7.4.2.2", {"start": v(5, 48.2) * mm, "end": v(9.25, 45.76) * mm});
            skLineSegment(sketch, "E7.4.2.3", {"start": v(0.75, 45.76) * mm, "end": v(5, 48.2) * mm});
            skLineSegment(sketch, "E7.4.2.4", {"start": v(0.75, 40.85) * mm, "end": v(0.75, 45.76) * mm});
            skLineSegment(sketch, "E7.4.2.5", {"start": v(5, 38.4) * mm, "end": v(0.75, 40.85) * mm});
            skLineSegment(sketch, "E7.4.3.0", {"start": v(9.25, 58.17) * mm, "end": v(5, 55.71) * mm});
            skLineSegment(sketch, "E7.4.3.1", {"start": v(9.25, 63.08) * mm, "end": v(9.25, 58.17) * mm});
            skLineSegment(sketch, "E7.4.3.2", {"start": v(5, 65.53) * mm, "end": v(9.25, 63.08) * mm});
            skLineSegment(sketch, "E7.4.3.3", {"start": v(0.75, 63.08) * mm, "end": v(5, 65.53) * mm});
            skLineSegment(sketch, "E7.4.3.4", {"start": v(0.75, 58.17) * mm, "end": v(0.75, 63.08) * mm});
            skLineSegment(sketch, "E7.4.3.5", {"start": v(5, 55.71) * mm, "end": v(0.75, 58.17) * mm});
            skLineSegment(sketch, "E7.4.4.0", {"start": v(9.25, 75.49) * mm, "end": v(5, 73.03) * mm});
            skLineSegment(sketch, "E7.4.4.1", {"start": v(9.25, 80.4) * mm, "end": v(9.25, 75.49) * mm});
            skLineSegment(sketch, "E7.4.4.2", {"start": v(5, 82.85) * mm, "end": v(9.25, 80.4) * mm});
            skLineSegment(sketch, "E7.4.4.3", {"start": v(0.75, 80.4) * mm, "end": v(5, 82.85) * mm});
            skLineSegment(sketch, "E7.4.4.4", {"start": v(0.75, 75.49) * mm, "end": v(0.75, 80.4) * mm});
            skLineSegment(sketch, "E7.4.4.5", {"start": v(5, 73.03) * mm, "end": v(0.75, 75.49) * mm});
            skLineSegment(sketch, "E7.5.0.0", {"start": v(19.25, 6.2) * mm, "end": v(15, 3.75) * mm});
            skLineSegment(sketch, "E7.5.0.1", {"start": v(19.25, 11.11) * mm, "end": v(19.25, 6.2) * mm});
            skLineSegment(sketch, "E7.5.0.2", {"start": v(15, 13.57) * mm, "end": v(19.25, 11.11) * mm});
            skLineSegment(sketch, "E7.5.0.3", {"start": v(10.75, 11.11) * mm, "end": v(15, 13.57) * mm});
            skLineSegment(sketch, "E7.5.0.4", {"start": v(10.75, 6.2) * mm, "end": v(10.75, 11.11) * mm});
            skLineSegment(sketch, "E7.5.0.5", {"start": v(15, 3.75) * mm, "end": v(10.75, 6.2) * mm});
            skLineSegment(sketch, "E7.5.1.0", {"start": v(19.25, 23.53) * mm, "end": v(15, 21.07) * mm});
            skLineSegment(sketch, "E7.5.1.1", {"start": v(19.25, 28.43) * mm, "end": v(19.25, 23.53) * mm});
            skLineSegment(sketch, "E7.5.1.2", {"start": v(15, 30.89) * mm, "end": v(19.25, 28.43) * mm});
            skLineSegment(sketch, "E7.5.1.3", {"start": v(10.75, 28.43) * mm, "end": v(15, 30.89) * mm});
            skLineSegment(sketch, "E7.5.1.4", {"start": v(10.75, 23.53) * mm, "end": v(10.75, 28.43) * mm});
            skLineSegment(sketch, "E7.5.1.5", {"start": v(15, 21.07) * mm, "end": v(10.75, 23.53) * mm});
            skLineSegment(sketch, "E7.5.2.0", {"start": v(19.25, 40.85) * mm, "end": v(15, 38.4) * mm});
            skLineSegment(sketch, "E7.5.2.1", {"start": v(19.25, 45.76) * mm, "end": v(19.25, 40.85) * mm});
            skLineSegment(sketch, "E7.5.2.2", {"start": v(15, 48.2) * mm, "end": v(19.25, 45.76) * mm});
            skLineSegment(sketch, "E7.5.2.3", {"start": v(10.75, 45.76) * mm, "end": v(15, 48.2) * mm});
            skLineSegment(sketch, "E7.5.2.4", {"start": v(10.75, 40.85) * mm, "end": v(10.75, 45.76) * mm});
            skLineSegment(sketch, "E7.5.2.5", {"start": v(15, 38.4) * mm, "end": v(10.75, 40.85) * mm});
            skLineSegment(sketch, "E7.5.3.0", {"start": v(19.25, 58.17) * mm, "end": v(15, 55.71) * mm});
            skLineSegment(sketch, "E7.5.3.1", {"start": v(19.25, 63.08) * mm, "end": v(19.25, 58.17) * mm});
            skLineSegment(sketch, "E7.5.3.2", {"start": v(15, 65.53) * mm, "end": v(19.25, 63.08) * mm});
            skLineSegment(sketch, "E7.5.3.3", {"start": v(10.75, 63.08) * mm, "end": v(15, 65.53) * mm});
            skLineSegment(sketch, "E7.5.3.4", {"start": v(10.75, 58.17) * mm, "end": v(10.75, 63.08) * mm});
            skLineSegment(sketch, "E7.5.3.5", {"start": v(15, 55.71) * mm, "end": v(10.75, 58.17) * mm});
            skLineSegment(sketch, "E7.5.4.0", {"start": v(19.25, 75.49) * mm, "end": v(15, 73.03) * mm});
            skLineSegment(sketch, "E7.5.4.1", {"start": v(19.25, 80.4) * mm, "end": v(19.25, 75.49) * mm});
            skLineSegment(sketch, "E7.5.4.2", {"start": v(15, 82.85) * mm, "end": v(19.25, 80.4) * mm});
            skLineSegment(sketch, "E7.5.4.3", {"start": v(10.75, 80.4) * mm, "end": v(15, 82.85) * mm});
            skLineSegment(sketch, "E7.5.4.4", {"start": v(10.75, 75.49) * mm, "end": v(10.75, 80.4) * mm});
            skLineSegment(sketch, "E7.5.4.5", {"start": v(15, 73.03) * mm, "end": v(10.75, 75.49) * mm});
            skLineSegment(sketch, "E7.6.0.0", {"start": v(29.25, 6.2) * mm, "end": v(25, 3.75) * mm});
            skLineSegment(sketch, "E7.6.0.1", {"start": v(29.25, 11.11) * mm, "end": v(29.25, 6.2) * mm});
            skLineSegment(sketch, "E7.6.0.2", {"start": v(25, 13.57) * mm, "end": v(29.25, 11.11) * mm});
            skLineSegment(sketch, "E7.6.0.3", {"start": v(20.75, 11.11) * mm, "end": v(25, 13.57) * mm});
            skLineSegment(sketch, "E7.6.0.4", {"start": v(20.75, 6.2) * mm, "end": v(20.75, 11.11) * mm});
            skLineSegment(sketch, "E7.6.0.5", {"start": v(25, 3.75) * mm, "end": v(20.75, 6.2) * mm});
            skLineSegment(sketch, "E7.6.1.0", {"start": v(29.25, 23.53) * mm, "end": v(25, 21.07) * mm});
            skLineSegment(sketch, "E7.6.1.1", {"start": v(29.25, 28.43) * mm, "end": v(29.25, 23.53) * mm});
            skLineSegment(sketch, "E7.6.1.2", {"start": v(25, 30.89) * mm, "end": v(29.25, 28.43) * mm});
            skLineSegment(sketch, "E7.6.1.3", {"start": v(20.75, 28.43) * mm, "end": v(25, 30.89) * mm});
            skLineSegment(sketch, "E7.6.1.4", {"start": v(20.75, 23.53) * mm, "end": v(20.75, 28.43) * mm});
            skLineSegment(sketch, "E7.6.1.5", {"start": v(25, 21.07) * mm, "end": v(20.75, 23.53) * mm});
            skLineSegment(sketch, "E7.6.2.0", {"start": v(29.25, 40.85) * mm, "end": v(25, 38.4) * mm});
            skLineSegment(sketch, "E7.6.2.1", {"start": v(29.25, 45.76) * mm, "end": v(29.25, 40.85) * mm});
            skLineSegment(sketch, "E7.6.2.2", {"start": v(25, 48.2) * mm, "end": v(29.25, 45.76) * mm});
            skLineSegment(sketch, "E7.6.2.3", {"start": v(20.75, 45.76) * mm, "end": v(25, 48.2) * mm});
            skLineSegment(sketch, "E7.6.2.4", {"start": v(20.75, 40.85) * mm, "end": v(20.75, 45.76) * mm});
            skLineSegment(sketch, "E7.6.2.5", {"start": v(25, 38.4) * mm, "end": v(20.75, 40.85) * mm});
            skLineSegment(sketch, "E7.6.3.0", {"start": v(29.25, 58.17) * mm, "end": v(25, 55.71) * mm});
            skLineSegment(sketch, "E7.6.3.1", {"start": v(29.25, 63.08) * mm, "end": v(29.25, 58.17) * mm});
            skLineSegment(sketch, "E7.6.3.2", {"start": v(25, 65.53) * mm, "end": v(29.25, 63.08) * mm});
            skLineSegment(sketch, "E7.6.3.3", {"start": v(20.75, 63.08) * mm, "end": v(25, 65.53) * mm});
            skLineSegment(sketch, "E7.6.3.4", {"start": v(20.75, 58.17) * mm, "end": v(20.75, 63.08) * mm});
            skLineSegment(sketch, "E7.6.3.5", {"start": v(25, 55.71) * mm, "end": v(20.75, 58.17) * mm});
            skLineSegment(sketch, "E7.6.4.0", {"start": v(29.25, 75.49) * mm, "end": v(25, 73.03) * mm});
            skLineSegment(sketch, "E7.6.4.1", {"start": v(29.25, 80.4) * mm, "end": v(29.25, 75.49) * mm});
            skLineSegment(sketch, "E7.6.4.2", {"start": v(25, 82.85) * mm, "end": v(29.25, 80.4) * mm});
            skLineSegment(sketch, "E7.6.4.3", {"start": v(20.75, 80.4) * mm, "end": v(25, 82.85) * mm});
            skLineSegment(sketch, "E7.6.4.4", {"start": v(20.75, 75.49) * mm, "end": v(20.75, 80.4) * mm});
            skLineSegment(sketch, "E7.6.4.5", {"start": v(25, 73.03) * mm, "end": v(20.75, 75.49) * mm});
            skLineSegment(sketch, "E7.7.0.0", {"start": v(39.25, 6.2) * mm, "end": v(35, 3.75) * mm});
            skLineSegment(sketch, "E7.7.0.1", {"start": v(39.25, 11.11) * mm, "end": v(39.25, 6.2) * mm});
            skLineSegment(sketch, "E7.7.0.2", {"start": v(35, 13.57) * mm, "end": v(39.25, 11.11) * mm});
            skLineSegment(sketch, "E7.7.0.3", {"start": v(30.75, 11.11) * mm, "end": v(35, 13.57) * mm});
            skLineSegment(sketch, "E7.7.0.4", {"start": v(30.75, 6.2) * mm, "end": v(30.75, 11.11) * mm});
            skLineSegment(sketch, "E7.7.0.5", {"start": v(35, 3.75) * mm, "end": v(30.75, 6.2) * mm});
            skLineSegment(sketch, "E7.7.1.0", {"start": v(39.25, 23.53) * mm, "end": v(35, 21.07) * mm});
            skLineSegment(sketch, "E7.7.1.1", {"start": v(39.25, 28.43) * mm, "end": v(39.25, 23.53) * mm});
            skLineSegment(sketch, "E7.7.1.2", {"start": v(35, 30.89) * mm, "end": v(39.25, 28.43) * mm});
            skLineSegment(sketch, "E7.7.1.3", {"start": v(30.75, 28.43) * mm, "end": v(35, 30.89) * mm});
            skLineSegment(sketch, "E7.7.1.4", {"start": v(30.75, 23.53) * mm, "end": v(30.75, 28.43) * mm});
            skLineSegment(sketch, "E7.7.1.5", {"start": v(35, 21.07) * mm, "end": v(30.75, 23.53) * mm});
            skLineSegment(sketch, "E7.7.2.0", {"start": v(39.25, 40.85) * mm, "end": v(35, 38.4) * mm});
            skLineSegment(sketch, "E7.7.2.1", {"start": v(39.25, 45.76) * mm, "end": v(39.25, 40.85) * mm});
            skLineSegment(sketch, "E7.7.2.2", {"start": v(35, 48.2) * mm, "end": v(39.25, 45.76) * mm});
            skLineSegment(sketch, "E7.7.2.3", {"start": v(30.75, 45.76) * mm, "end": v(35, 48.2) * mm});
            skLineSegment(sketch, "E7.7.2.4", {"start": v(30.75, 40.85) * mm, "end": v(30.75, 45.76) * mm});
            skLineSegment(sketch, "E7.7.2.5", {"start": v(35, 38.4) * mm, "end": v(30.75, 40.85) * mm});
            skLineSegment(sketch, "E7.7.3.0", {"start": v(39.25, 58.17) * mm, "end": v(35, 55.71) * mm});
            skLineSegment(sketch, "E7.7.3.1", {"start": v(39.25, 63.08) * mm, "end": v(39.25, 58.17) * mm});
            skLineSegment(sketch, "E7.7.3.2", {"start": v(35, 65.53) * mm, "end": v(39.25, 63.08) * mm});
            skLineSegment(sketch, "E7.7.3.3", {"start": v(30.75, 63.08) * mm, "end": v(35, 65.53) * mm});
            skLineSegment(sketch, "E7.7.3.4", {"start": v(30.75, 58.17) * mm, "end": v(30.75, 63.08) * mm});
            skLineSegment(sketch, "E7.7.3.5", {"start": v(35, 55.71) * mm, "end": v(30.75, 58.17) * mm});
            skLineSegment(sketch, "E7.7.4.0", {"start": v(39.25, 75.49) * mm, "end": v(35, 73.03) * mm});
            skLineSegment(sketch, "E7.7.4.1", {"start": v(39.25, 80.4) * mm, "end": v(39.25, 75.49) * mm});
            skLineSegment(sketch, "E7.7.4.2", {"start": v(35, 82.85) * mm, "end": v(39.25, 80.4) * mm});
            skLineSegment(sketch, "E7.7.4.3", {"start": v(30.75, 80.4) * mm, "end": v(35, 82.85) * mm});
            skLineSegment(sketch, "E7.7.4.4", {"start": v(30.75, 75.49) * mm, "end": v(30.75, 80.4) * mm});
            skLineSegment(sketch, "E7.7.4.5", {"start": v(35, 73.03) * mm, "end": v(30.75, 75.49) * mm});
            skLineSegment(sketch, "E7.direction1", {"start": v(-39.25, 6.2) * mm, "end": v(-29.25, 6.2) * mm, "construction": true});
            skLineSegment(sketch, "E7.direction2", {"start": v(-39.25, 6.2) * mm, "end": v(-39.25, 23.53) * mm, "construction": true});
            skLineSegment(sketch, "E8.0.0.5", {"start": v(-30.75, 92.8) * mm, "end": v(-35, 90.36) * mm});
            skLineSegment(sketch, "E8.3.0.5", {"start": v(-30.75, 97.72) * mm, "end": v(-30.75, 92.8) * mm});
            skLineSegment(sketch, "E8.6.0.5", {"start": v(-35, 100.17) * mm, "end": v(-30.75, 97.72) * mm});
            skLineSegment(sketch, "E8.9.0.5", {"start": v(-39.25, 97.72) * mm, "end": v(-35, 100.17) * mm});
            skLineSegment(sketch, "E8.12.0.5", {"start": v(-39.25, 92.8) * mm, "end": v(-39.25, 97.72) * mm});
            skLineSegment(sketch, "E8.15.0.5", {"start": v(-35, 90.36) * mm, "end": v(-39.25, 92.8) * mm});
            skLineSegment(sketch, "E8.0.0.6", {"start": v(-30.75, 110.13) * mm, "end": v(-35, 107.68) * mm});
            skLineSegment(sketch, "E8.3.0.6", {"start": v(-30.75, 115.04) * mm, "end": v(-30.75, 110.13) * mm});
            skLineSegment(sketch, "E8.6.0.6", {"start": v(-35, 117.5) * mm, "end": v(-30.75, 115.04) * mm});
            skLineSegment(sketch, "E8.9.0.6", {"start": v(-39.25, 115.04) * mm, "end": v(-35, 117.5) * mm});
            skLineSegment(sketch, "E8.12.0.6", {"start": v(-39.25, 110.13) * mm, "end": v(-39.25, 115.04) * mm});
            skLineSegment(sketch, "E8.15.0.6", {"start": v(-35, 107.68) * mm, "end": v(-39.25, 110.13) * mm});
            skLineSegment(sketch, "E8.0.0.7", {"start": v(-30.75, 127.45) * mm, "end": v(-35, 125) * mm});
            skLineSegment(sketch, "E8.3.0.7", {"start": v(-30.75, 132.36) * mm, "end": v(-30.75, 127.45) * mm});
            skLineSegment(sketch, "E8.6.0.7", {"start": v(-35, 134.81) * mm, "end": v(-30.75, 132.36) * mm});
            skLineSegment(sketch, "E8.9.0.7", {"start": v(-39.25, 132.36) * mm, "end": v(-35, 134.81) * mm});
            skLineSegment(sketch, "E8.12.0.7", {"start": v(-39.25, 127.45) * mm, "end": v(-39.25, 132.36) * mm});
            skLineSegment(sketch, "E8.15.0.7", {"start": v(-35, 125) * mm, "end": v(-39.25, 127.45) * mm});
            skLineSegment(sketch, "E8.0.1.5", {"start": v(-20.75, 92.8) * mm, "end": v(-25, 90.36) * mm});
            skLineSegment(sketch, "E8.3.1.5", {"start": v(-20.75, 97.72) * mm, "end": v(-20.75, 92.8) * mm});
            skLineSegment(sketch, "E8.6.1.5", {"start": v(-25, 100.17) * mm, "end": v(-20.75, 97.72) * mm});
            skLineSegment(sketch, "E8.9.1.5", {"start": v(-29.25, 97.72) * mm, "end": v(-25, 100.17) * mm});
            skLineSegment(sketch, "E8.12.1.5", {"start": v(-29.25, 92.8) * mm, "end": v(-29.25, 97.72) * mm});
            skLineSegment(sketch, "E8.15.1.5", {"start": v(-25, 90.36) * mm, "end": v(-29.25, 92.8) * mm});
            skLineSegment(sketch, "E8.0.1.6", {"start": v(-20.75, 110.13) * mm, "end": v(-25, 107.68) * mm});
            skLineSegment(sketch, "E8.3.1.6", {"start": v(-20.75, 115.04) * mm, "end": v(-20.75, 110.13) * mm});
            skLineSegment(sketch, "E8.6.1.6", {"start": v(-25, 117.5) * mm, "end": v(-20.75, 115.04) * mm});
            skLineSegment(sketch, "E8.9.1.6", {"start": v(-29.25, 115.04) * mm, "end": v(-25, 117.5) * mm});
            skLineSegment(sketch, "E8.12.1.6", {"start": v(-29.25, 110.13) * mm, "end": v(-29.25, 115.04) * mm});
            skLineSegment(sketch, "E8.15.1.6", {"start": v(-25, 107.68) * mm, "end": v(-29.25, 110.13) * mm});
            skLineSegment(sketch, "E8.0.1.7", {"start": v(-20.75, 127.45) * mm, "end": v(-25, 125) * mm});
            skLineSegment(sketch, "E8.3.1.7", {"start": v(-20.75, 132.36) * mm, "end": v(-20.75, 127.45) * mm});
            skLineSegment(sketch, "E8.6.1.7", {"start": v(-25, 134.81) * mm, "end": v(-20.75, 132.36) * mm});
            skLineSegment(sketch, "E8.9.1.7", {"start": v(-29.25, 132.36) * mm, "end": v(-25, 134.81) * mm});
            skLineSegment(sketch, "E8.12.1.7", {"start": v(-29.25, 127.45) * mm, "end": v(-29.25, 132.36) * mm});
            skLineSegment(sketch, "E8.15.1.7", {"start": v(-25, 125) * mm, "end": v(-29.25, 127.45) * mm});
            skLineSegment(sketch, "E8.0.2.5", {"start": v(-10.75, 92.8) * mm, "end": v(-15, 90.36) * mm});
            skLineSegment(sketch, "E8.3.2.5", {"start": v(-10.75, 97.72) * mm, "end": v(-10.75, 92.8) * mm});
            skLineSegment(sketch, "E8.6.2.5", {"start": v(-15, 100.17) * mm, "end": v(-10.75, 97.72) * mm});
            skLineSegment(sketch, "E8.9.2.5", {"start": v(-19.25, 97.72) * mm, "end": v(-15, 100.17) * mm});
            skLineSegment(sketch, "E8.12.2.5", {"start": v(-19.25, 92.8) * mm, "end": v(-19.25, 97.72) * mm});
            skLineSegment(sketch, "E8.15.2.5", {"start": v(-15, 90.36) * mm, "end": v(-19.25, 92.8) * mm});
            skLineSegment(sketch, "E8.0.2.6", {"start": v(-10.75, 110.13) * mm, "end": v(-15, 107.68) * mm});
            skLineSegment(sketch, "E8.3.2.6", {"start": v(-10.75, 115.04) * mm, "end": v(-10.75, 110.13) * mm});
            skLineSegment(sketch, "E8.6.2.6", {"start": v(-15, 117.5) * mm, "end": v(-10.75, 115.04) * mm});
            skLineSegment(sketch, "E8.9.2.6", {"start": v(-19.25, 115.04) * mm, "end": v(-15, 117.5) * mm});
            skLineSegment(sketch, "E8.12.2.6", {"start": v(-19.25, 110.13) * mm, "end": v(-19.25, 115.04) * mm});
            skLineSegment(sketch, "E8.15.2.6", {"start": v(-15, 107.68) * mm, "end": v(-19.25, 110.13) * mm});
            skLineSegment(sketch, "E8.0.2.7", {"start": v(-10.75, 127.45) * mm, "end": v(-15, 125) * mm});
            skLineSegment(sketch, "E8.3.2.7", {"start": v(-10.75, 132.36) * mm, "end": v(-10.75, 127.45) * mm});
            skLineSegment(sketch, "E8.6.2.7", {"start": v(-15, 134.81) * mm, "end": v(-10.75, 132.36) * mm});
            skLineSegment(sketch, "E8.9.2.7", {"start": v(-19.25, 132.36) * mm, "end": v(-15, 134.81) * mm});
            skLineSegment(sketch, "E8.12.2.7", {"start": v(-19.25, 127.45) * mm, "end": v(-19.25, 132.36) * mm});
            skLineSegment(sketch, "E8.15.2.7", {"start": v(-15, 125) * mm, "end": v(-19.25, 127.45) * mm});
            skLineSegment(sketch, "E8.0.3.5", {"start": v(-0.75, 92.8) * mm, "end": v(-5, 90.36) * mm});
            skLineSegment(sketch, "E8.3.3.5", {"start": v(-0.75, 97.72) * mm, "end": v(-0.75, 92.8) * mm});
            skLineSegment(sketch, "E8.6.3.5", {"start": v(-5, 100.17) * mm, "end": v(-0.75, 97.72) * mm});
            skLineSegment(sketch, "E8.9.3.5", {"start": v(-9.25, 97.72) * mm, "end": v(-5, 100.17) * mm});
            skLineSegment(sketch, "E8.12.3.5", {"start": v(-9.25, 92.8) * mm, "end": v(-9.25, 97.72) * mm});
            skLineSegment(sketch, "E8.15.3.5", {"start": v(-5, 90.36) * mm, "end": v(-9.25, 92.8) * mm});
            skLineSegment(sketch, "E8.0.3.6", {"start": v(-0.75, 110.13) * mm, "end": v(-5, 107.68) * mm});
            skLineSegment(sketch, "E8.3.3.6", {"start": v(-0.75, 115.04) * mm, "end": v(-0.75, 110.13) * mm});
            skLineSegment(sketch, "E8.6.3.6", {"start": v(-5, 117.5) * mm, "end": v(-0.75, 115.04) * mm});
            skLineSegment(sketch, "E8.9.3.6", {"start": v(-9.25, 115.04) * mm, "end": v(-5, 117.5) * mm});
            skLineSegment(sketch, "E8.12.3.6", {"start": v(-9.25, 110.13) * mm, "end": v(-9.25, 115.04) * mm});
            skLineSegment(sketch, "E8.15.3.6", {"start": v(-5, 107.68) * mm, "end": v(-9.25, 110.13) * mm});
            skLineSegment(sketch, "E8.0.3.7", {"start": v(-0.75, 127.45) * mm, "end": v(-5, 125) * mm});
            skLineSegment(sketch, "E8.3.3.7", {"start": v(-0.75, 132.36) * mm, "end": v(-0.75, 127.45) * mm});
            skLineSegment(sketch, "E8.6.3.7", {"start": v(-5, 134.81) * mm, "end": v(-0.75, 132.36) * mm});
            skLineSegment(sketch, "E8.9.3.7", {"start": v(-9.25, 132.36) * mm, "end": v(-5, 134.81) * mm});
            skLineSegment(sketch, "E8.12.3.7", {"start": v(-9.25, 127.45) * mm, "end": v(-9.25, 132.36) * mm});
            skLineSegment(sketch, "E8.15.3.7", {"start": v(-5, 125) * mm, "end": v(-9.25, 127.45) * mm});
            skLineSegment(sketch, "E8.0.4.5", {"start": v(9.25, 92.8) * mm, "end": v(5, 90.36) * mm});
            skLineSegment(sketch, "E8.3.4.5", {"start": v(9.25, 97.72) * mm, "end": v(9.25, 92.8) * mm});
            skLineSegment(sketch, "E8.6.4.5", {"start": v(5, 100.17) * mm, "end": v(9.25, 97.72) * mm});
            skLineSegment(sketch, "E8.9.4.5", {"start": v(0.75, 97.72) * mm, "end": v(5, 100.17) * mm});
            skLineSegment(sketch, "E8.12.4.5", {"start": v(0.75, 92.8) * mm, "end": v(0.75, 97.72) * mm});
            skLineSegment(sketch, "E8.15.4.5", {"start": v(5, 90.36) * mm, "end": v(0.75, 92.8) * mm});
            skLineSegment(sketch, "E8.0.4.6", {"start": v(9.25, 110.13) * mm, "end": v(5, 107.68) * mm});
            skLineSegment(sketch, "E8.3.4.6", {"start": v(9.25, 115.04) * mm, "end": v(9.25, 110.13) * mm});
            skLineSegment(sketch, "E8.6.4.6", {"start": v(5, 117.5) * mm, "end": v(9.25, 115.04) * mm});
            skLineSegment(sketch, "E8.9.4.6", {"start": v(0.75, 115.04) * mm, "end": v(5, 117.5) * mm});
            skLineSegment(sketch, "E8.12.4.6", {"start": v(0.75, 110.13) * mm, "end": v(0.75, 115.04) * mm});
            skLineSegment(sketch, "E8.15.4.6", {"start": v(5, 107.68) * mm, "end": v(0.75, 110.13) * mm});
            skLineSegment(sketch, "E8.0.4.7", {"start": v(9.25, 127.45) * mm, "end": v(5, 125) * mm});
            skLineSegment(sketch, "E8.3.4.7", {"start": v(9.25, 132.36) * mm, "end": v(9.25, 127.45) * mm});
            skLineSegment(sketch, "E8.6.4.7", {"start": v(5, 134.81) * mm, "end": v(9.25, 132.36) * mm});
            skLineSegment(sketch, "E8.9.4.7", {"start": v(0.75, 132.36) * mm, "end": v(5, 134.81) * mm});
            skLineSegment(sketch, "E8.12.4.7", {"start": v(0.75, 127.45) * mm, "end": v(0.75, 132.36) * mm});
            skLineSegment(sketch, "E8.15.4.7", {"start": v(5, 125) * mm, "end": v(0.75, 127.45) * mm});
            skLineSegment(sketch, "E8.0.5.5", {"start": v(19.25, 92.8) * mm, "end": v(15, 90.36) * mm});
            skLineSegment(sketch, "E8.3.5.5", {"start": v(19.25, 97.72) * mm, "end": v(19.25, 92.8) * mm});
            skLineSegment(sketch, "E8.6.5.5", {"start": v(15, 100.17) * mm, "end": v(19.25, 97.72) * mm});
            skLineSegment(sketch, "E8.9.5.5", {"start": v(10.75, 97.72) * mm, "end": v(15, 100.17) * mm});
            skLineSegment(sketch, "E8.12.5.5", {"start": v(10.75, 92.8) * mm, "end": v(10.75, 97.72) * mm});
            skLineSegment(sketch, "E8.15.5.5", {"start": v(15, 90.36) * mm, "end": v(10.75, 92.8) * mm});
            skLineSegment(sketch, "E8.0.5.6", {"start": v(19.25, 110.13) * mm, "end": v(15, 107.68) * mm});
            skLineSegment(sketch, "E8.3.5.6", {"start": v(19.25, 115.04) * mm, "end": v(19.25, 110.13) * mm});
            skLineSegment(sketch, "E8.6.5.6", {"start": v(15, 117.5) * mm, "end": v(19.25, 115.04) * mm});
            skLineSegment(sketch, "E8.9.5.6", {"start": v(10.75, 115.04) * mm, "end": v(15, 117.5) * mm});
            skLineSegment(sketch, "E8.12.5.6", {"start": v(10.75, 110.13) * mm, "end": v(10.75, 115.04) * mm});
            skLineSegment(sketch, "E8.15.5.6", {"start": v(15, 107.68) * mm, "end": v(10.75, 110.13) * mm});
            skLineSegment(sketch, "E8.0.5.7", {"start": v(19.25, 127.45) * mm, "end": v(15, 125) * mm});
            skLineSegment(sketch, "E8.3.5.7", {"start": v(19.25, 132.36) * mm, "end": v(19.25, 127.45) * mm});
            skLineSegment(sketch, "E8.6.5.7", {"start": v(15, 134.81) * mm, "end": v(19.25, 132.36) * mm});
            skLineSegment(sketch, "E8.9.5.7", {"start": v(10.75, 132.36) * mm, "end": v(15, 134.81) * mm});
            skLineSegment(sketch, "E8.12.5.7", {"start": v(10.75, 127.45) * mm, "end": v(10.75, 132.36) * mm});
            skLineSegment(sketch, "E8.15.5.7", {"start": v(15, 125) * mm, "end": v(10.75, 127.45) * mm});
            skLineSegment(sketch, "E8.0.6.5", {"start": v(29.25, 92.8) * mm, "end": v(25, 90.36) * mm});
            skLineSegment(sketch, "E8.3.6.5", {"start": v(29.25, 97.72) * mm, "end": v(29.25, 92.8) * mm});
            skLineSegment(sketch, "E8.6.6.5", {"start": v(25, 100.17) * mm, "end": v(29.25, 97.72) * mm});
            skLineSegment(sketch, "E8.9.6.5", {"start": v(20.75, 97.72) * mm, "end": v(25, 100.17) * mm});
            skLineSegment(sketch, "E8.12.6.5", {"start": v(20.75, 92.8) * mm, "end": v(20.75, 97.72) * mm});
            skLineSegment(sketch, "E8.15.6.5", {"start": v(25, 90.36) * mm, "end": v(20.75, 92.8) * mm});
            skLineSegment(sketch, "E8.0.6.6", {"start": v(29.25, 110.13) * mm, "end": v(25, 107.68) * mm});
            skLineSegment(sketch, "E8.3.6.6", {"start": v(29.25, 115.04) * mm, "end": v(29.25, 110.13) * mm});
            skLineSegment(sketch, "E8.6.6.6", {"start": v(25, 117.5) * mm, "end": v(29.25, 115.04) * mm});
            skLineSegment(sketch, "E8.9.6.6", {"start": v(20.75, 115.04) * mm, "end": v(25, 117.5) * mm});
            skLineSegment(sketch, "E8.12.6.6", {"start": v(20.75, 110.13) * mm, "end": v(20.75, 115.04) * mm});
            skLineSegment(sketch, "E8.15.6.6", {"start": v(25, 107.68) * mm, "end": v(20.75, 110.13) * mm});
            skLineSegment(sketch, "E8.0.6.7", {"start": v(29.25, 127.45) * mm, "end": v(25, 125) * mm});
            skLineSegment(sketch, "E8.3.6.7", {"start": v(29.25, 132.36) * mm, "end": v(29.25, 127.45) * mm});
            skLineSegment(sketch, "E8.6.6.7", {"start": v(25, 134.81) * mm, "end": v(29.25, 132.36) * mm});
            skLineSegment(sketch, "E8.9.6.7", {"start": v(20.75, 132.36) * mm, "end": v(25, 134.81) * mm});
            skLineSegment(sketch, "E8.12.6.7", {"start": v(20.75, 127.45) * mm, "end": v(20.75, 132.36) * mm});
            skLineSegment(sketch, "E8.15.6.7", {"start": v(25, 125) * mm, "end": v(20.75, 127.45) * mm});
            skLineSegment(sketch, "E8.0.7.5", {"start": v(39.25, 92.8) * mm, "end": v(35, 90.36) * mm});
            skLineSegment(sketch, "E8.3.7.5", {"start": v(39.25, 97.72) * mm, "end": v(39.25, 92.8) * mm});
            skLineSegment(sketch, "E8.6.7.5", {"start": v(35, 100.17) * mm, "end": v(39.25, 97.72) * mm});
            skLineSegment(sketch, "E8.9.7.5", {"start": v(30.75, 97.72) * mm, "end": v(35, 100.17) * mm});
            skLineSegment(sketch, "E8.12.7.5", {"start": v(30.75, 92.8) * mm, "end": v(30.75, 97.72) * mm});
            skLineSegment(sketch, "E8.15.7.5", {"start": v(35, 90.36) * mm, "end": v(30.75, 92.8) * mm});
            skLineSegment(sketch, "E8.0.7.6", {"start": v(39.25, 110.13) * mm, "end": v(35, 107.68) * mm});
            skLineSegment(sketch, "E8.3.7.6", {"start": v(39.25, 115.04) * mm, "end": v(39.25, 110.13) * mm});
            skLineSegment(sketch, "E8.6.7.6", {"start": v(35, 117.5) * mm, "end": v(39.25, 115.04) * mm});
            skLineSegment(sketch, "E8.9.7.6", {"start": v(30.75, 115.04) * mm, "end": v(35, 117.5) * mm});
            skLineSegment(sketch, "E8.12.7.6", {"start": v(30.75, 110.13) * mm, "end": v(30.75, 115.04) * mm});
            skLineSegment(sketch, "E8.15.7.6", {"start": v(35, 107.68) * mm, "end": v(30.75, 110.13) * mm});
            skLineSegment(sketch, "E8.0.7.7", {"start": v(39.25, 127.45) * mm, "end": v(35, 125) * mm});
            skLineSegment(sketch, "E8.3.7.7", {"start": v(39.25, 132.36) * mm, "end": v(39.25, 127.45) * mm});
            skLineSegment(sketch, "E8.6.7.7", {"start": v(35, 134.81) * mm, "end": v(39.25, 132.36) * mm});
            skLineSegment(sketch, "E8.9.7.7", {"start": v(30.75, 132.36) * mm, "end": v(35, 134.81) * mm});
            skLineSegment(sketch, "E8.12.7.7", {"start": v(30.75, 127.45) * mm, "end": v(30.75, 132.36) * mm});
            skLineSegment(sketch, "E8.15.7.7", {"start": v(35, 125) * mm, "end": v(30.75, 127.45) * mm});
            skSolve(sketch);
        }
        {
            var Q0;
            Q0 = qSketchRegion(id + "F2", true);
            extrude(context, id + "F3", {"entities" : qUnion([Q0]), "operationType" : NewBodyOperationType.REMOVE, "oppositeDirection" : true, "depth" : 4 * mm});
        }
        {
            var Q0;
            Q0=makeQuery(id+"F1.opExtrude","CAP_FACE",FACE,{"disambiguationData":[OSD([sQuery(id+"F0.wireOp",EDGE,"E0.0"),sQuery(id+"F0.wireOp",EDGE,"E0.1"),sQuery(id+"F0.wireOp",EDGE,"E0.2"),sQuery(id+"F0.wireOp",EDGE,"E0.3"),sQuery(id+"F0.wireOp",EDGE,"E0.4"),sQuery(id+"F0.wireOp",EDGE,"E0.5")])],"isStart":false});
            var sketch = newSketch(context, id + "F4", { "sketchPlane" : qUnion([Q0])});
            skCircle(sketch, "E9", {"center": v(0, 0) * mm, "radius": 69.28 * mm});
            skSolve(sketch);
        }
    });
